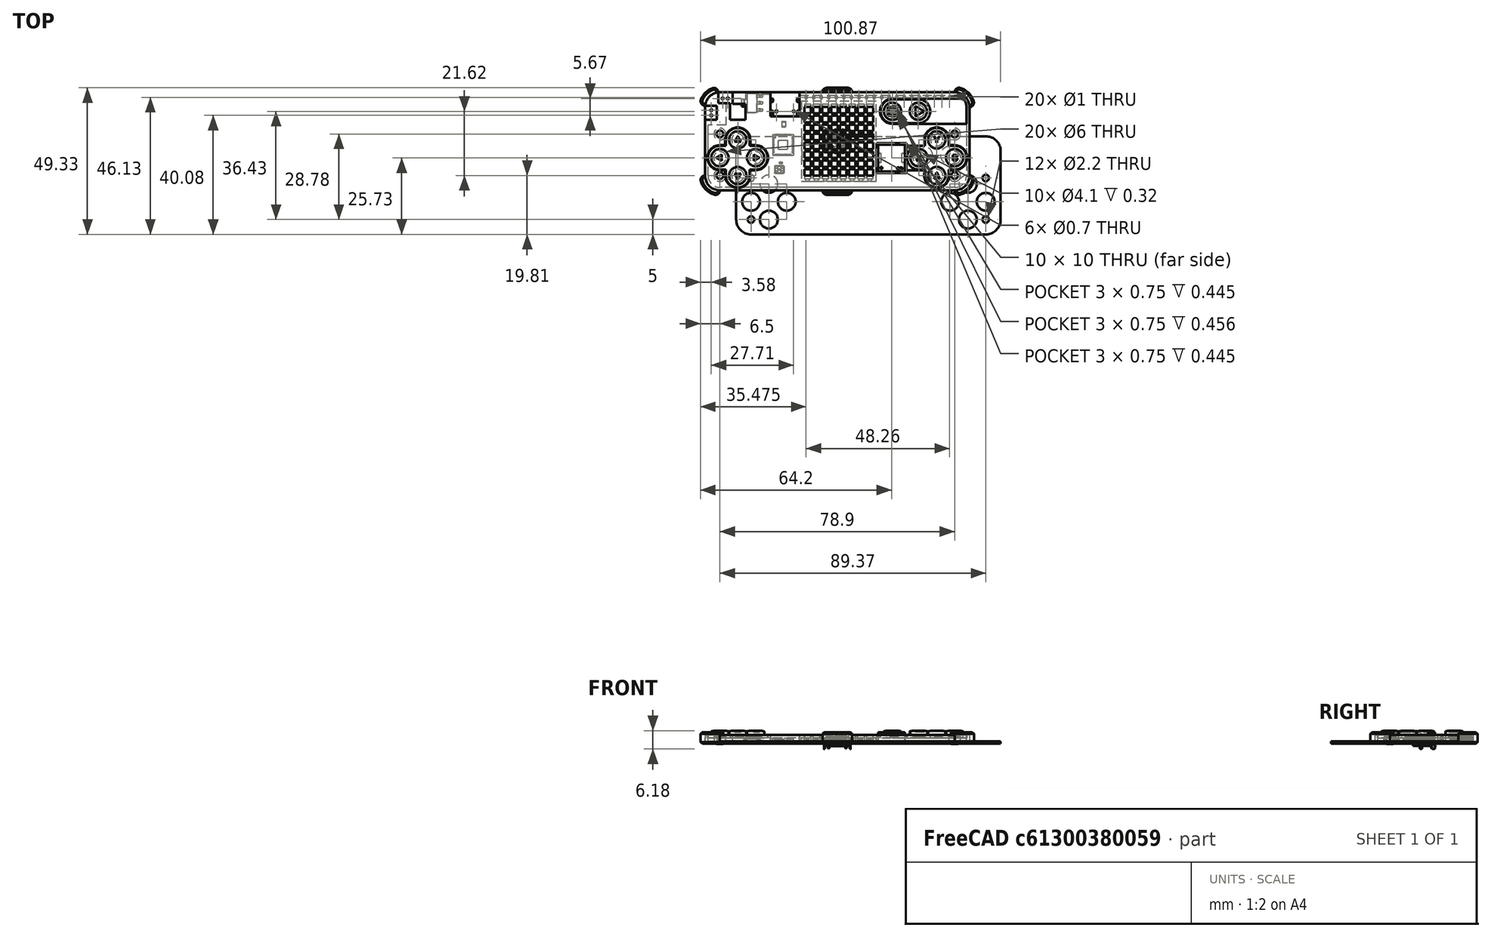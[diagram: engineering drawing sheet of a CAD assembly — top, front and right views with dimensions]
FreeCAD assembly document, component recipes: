
FREECAD ASSEMBLY — COMPONENT RECIPES ("PIX6T4_Color")

This assembly document has 8 components, labeled P0..P7 below (a component is one placed body or linked part). 4 of them carry a construction recipe — the FreeCAD feature program that regenerates the part from scratch, quoted from this document or its linked companion documents; the rest are supplied as boundary geometry only. No exploded tour is included for this assembly.
COMPONENT P0 — geometry summary ("PIX6T4_Color_top"; no construction recipe available for this part):
  bounding box: 88.9 x 33.0 x 0.8 mm
  tessellated surface: 7,652 triangles
  volume: 2030 mm^3 (86% of its bounding box)
  symmetry: mirror-symmetric across its z mid-plane
COMPONENT P1 — geometry summary ("PIX6T4_Color_top_Rev1"; no construction recipe available for this part):
  bounding box: 88.9 x 33.0 x 0.8 mm
  tessellated surface: 7,672 triangles
  volume: 1950 mm^3 (83% of its bounding box)
COMPONENT P2 — geometry summary ("PIX6T4_Color_Rev2"; no construction recipe available for this part):
  bounding box: 88.9 x 33.0 x 4.2 mm
  tessellated surface: 153,932 triangles
  volume: 3159 mm^3 (26% of its bounding box)
COMPONENT P3 — geometry summary ("PIX6T4_Color_Rev1"; no construction recipe available for this part):
  bounding box: 88.9 x 33.0 x 4.2 mm
  tessellated surface: 147,180 triangles
  volume: 3151 mm^3 (25% of its bounding box)
COMPONENT P4 — recipe-attached ("Body", modeled in this document).
Construction recipe (the document's own serialized feature program — sketch geometry with constraints, then the solid features built on it; lengths are millimeters unless a unit is written):

FEATURE [PartDesign::SubShapeBinder] Binder  label="Top of PCB Binder"
  BindCopyOnChange = 0
  BindMode = 0
  ClaimChildren = false
  Context = -> Body [Binder.]
  Fuse = false
  MakeFace = true
  OffsetFill = false
  OffsetIntersection = false
  OffsetJoinType = 0
  OffsetOpenResult = false
  PartialLoad = false
  Relative = true
  Support = -> [Board_e6d7[Board_Geoms_e6d7.Pcb_e6d7.Face63]]
  _Version = 2
FEATURE [PartDesign::Plane] DatumPlane
  AttachmentSupport = -> [Binder]
  Length = 105.452
  MapMode = 5
  ResizeMode = 0
  Width = 63.5569
FEATURE [PartDesign::SubShapeBinder] Binder001  label="Bottom of top binder"
  BindCopyOnChange = 0
  BindMode = 0
  ClaimChildren = false
  Context = -> Board_83e9 [Body.Binder001.]
  Fuse = false
  MakeFace = true
  OffsetFill = false
  OffsetIntersection = false
  OffsetJoinType = 0
  OffsetOpenResult = false
  PartialLoad = false
  Relative = true
  Support = -> [Board_83e9[Board_Geoms_83e9.Pcb_83e9.Face32]]
  _Version = 2
FEATURE [PartDesign::Plane] DatumPlane001
  AttachmentSupport = -> [Binder001]
  Length = 105.452
  MapMode = 5
  Placement = pos=(0,0,2.2) rot=(1,0,0;3.14159rad)
  ResizeMode = 0
  Width = 63.5569
FEATURE [Sketcher::SketchObject] Sketch001
  ArcFitTolerance = 1e-06
  AttachmentSupport = -> [DatumPlane001]
  ExternalGeometry = -> [Binder001]
  FullyConstrained = true
  MakeInternals = false
  MapMode = 5
  Placement = pos=(0,0,2.2) rot=(1,0,0;3.14159rad)
  sketch-geometry (44):
    g0: ArcOfCircle CenterX=18.55 CenterY=-10.11 CenterZ=0 NormalX=0 NormalY=0 NormalZ=1 AngleXU=0 Radius=4.2 StartAngle=1.5708 EndAngle=4.71239
    g1: ArcOfCircle CenterX=27.25 CenterY=-10.11 CenterZ=0 NormalX=0 NormalY=0 NormalZ=1 AngleXU=0 Radius=4.2 StartAngle=4.71239 EndAngle=7.85398
    g2: LineSegment StartX=18.55 StartY=-5.91 StartZ=0 EndX=27.25 EndY=-5.91 EndZ=0
    g3: LineSegment StartX=18.55 StartY=-14.31 StartZ=0 EndX=27.25 EndY=-14.31 EndZ=0
    g4: ArcOfCircle CenterX=-39.45 CenterY=5.51 CenterZ=0 NormalX=0 NormalY=0 NormalZ=1 AngleXU=0 Radius=4.2 StartAngle=1.5708 EndAngle=4.71239
    g5: ArcOfCircle CenterX=-33.45 CenterY=11.51 CenterZ=0 NormalX=0 NormalY=0 NormalZ=1 AngleXU=0 Radius=4.2 StartAngle=0 EndAngle=3.14159
    g6: ArcOfCircle CenterX=-27.45 CenterY=5.51 CenterZ=0 NormalX=0 NormalY=0 NormalZ=1 AngleXU=0 Radius=4.2 StartAngle=4.71239 EndAngle=7.85398
    g7: ArcOfCircle CenterX=-33.45 CenterY=-0.49 CenterZ=0 NormalX=0 NormalY=0 NormalZ=1 AngleXU=0 Radius=4.2 StartAngle=3.14159 EndAngle=6.28319
    g8: LineSegment StartX=-39.45 StartY=9.71 StartZ=0 EndX=-37.65 EndY=9.71 EndZ=0
    g9: LineSegment StartX=-37.65 StartY=9.71 StartZ=0 EndX=-37.65 EndY=11.51 EndZ=0
    g10: LineSegment StartX=-39.45 StartY=1.31 StartZ=0 EndX=-37.65 EndY=1.31 EndZ=0
    g11: LineSegment StartX=-37.65 StartY=1.31 StartZ=0 EndX=-37.65 EndY=-0.49 EndZ=0
    g12: LineSegment StartX=-29.25 StartY=-0.49 StartZ=0 EndX=-29.25 EndY=1.31 EndZ=0
    g13: LineSegment StartX=-29.25 StartY=1.31 StartZ=0 EndX=-27.45 EndY=1.31 EndZ=0
    g14: LineSegment StartX=-29.25 StartY=11.51 StartZ=0 EndX=-29.25 EndY=9.71 EndZ=0
    g15: LineSegment StartX=-29.25 StartY=9.71 StartZ=0 EndX=-27.45 EndY=9.71 EndZ=0
    g16: LineSegment StartX=-39.45 StartY=-16.51 StartZ=0 EndX=-22.45 EndY=-16.51 EndZ=0
    g17: LineSegment StartX=-22.45 StartY=-16.51 StartZ=0 EndX=-22.45 EndY=-8.46 EndZ=0
    g18: LineSegment StartX=-22.45 StartY=-8.46 StartZ=0 EndX=-12.65 EndY=-8.46 EndZ=0
    g19: LineSegment StartX=-12.65 StartY=-8.46 StartZ=0 EndX=-12.65 EndY=-16.51 EndZ=0
    g20: LineSegment StartX=-12.65 StartY=-16.51 StartZ=0 EndX=39.45 EndY=-16.51 EndZ=0
    g21: LineSegment StartX=-44.45 StartY=-11.51 StartZ=0 EndX=-44.45 EndY=11.51 EndZ=0
    g22: LineSegment StartX=-39.45 StartY=16.51 StartZ=0 EndX=39.45 EndY=16.51 EndZ=0
    g23: LineSegment StartX=13.25 StartY=10.59 StartZ=0 EndX=13.25 EndY=0.59 EndZ=0
    g24: LineSegment StartX=13.25 StartY=0.59 StartZ=0 EndX=23.25 EndY=0.59 EndZ=0
    g25: LineSegment StartX=23.25 StartY=10.59 StartZ=0 EndX=13.25 EndY=10.59 EndZ=0
    g26: LineSegment StartX=44.45 StartY=11.51 StartZ=0 EndX=44.45 EndY=-11.51 EndZ=0
    g27: ArcOfCircle CenterX=33.45 CenterY=11.51 CenterZ=0 NormalX=0 NormalY=0 NormalZ=1 AngleXU=0 Radius=4.2 StartAngle=1e-16 EndAngle=3.14159
    g28: ArcOfCircle CenterX=39.45 CenterY=5.51 CenterZ=0 NormalX=0 NormalY=0 NormalZ=1 AngleXU=0 Radius=4.2 StartAngle=4.71239 EndAngle=7.85398
    g29: ArcOfCircle CenterX=33.45 CenterY=-0.49 CenterZ=0 NormalX=0 NormalY=0 NormalZ=1 AngleXU=0 Radius=4.2 StartAngle=3.14159 EndAngle=6.28319
    g30: LineSegment StartX=23.25 StartY=9.71 StartZ=0 EndX=29.25 EndY=9.71 EndZ=0
    g31: LineSegment StartX=29.25 StartY=9.71 StartZ=0 EndX=29.25 EndY=11.51 EndZ=0
    g32: LineSegment StartX=37.65 StartY=11.51 StartZ=0 EndX=37.65 EndY=9.71 EndZ=0
    g33: LineSegment StartX=37.65 StartY=9.71 StartZ=0 EndX=39.45 EndY=9.71 EndZ=0
    g34: LineSegment StartX=39.45 StartY=1.31 StartZ=0 EndX=37.65 EndY=1.31 EndZ=0
    g35: LineSegment StartX=37.65 StartY=1.31 StartZ=0 EndX=37.65 EndY=-0.49 EndZ=0
    g36: LineSegment StartX=29.25 StartY=-0.49 StartZ=0 EndX=29.25 EndY=1.47 EndZ=0
    g37: LineSegment StartX=23.25 StartY=1.47 StartZ=0 EndX=29.25 EndY=1.47 EndZ=0
    g38: ArcOfCircle CenterX=-39.45 CenterY=11.51 CenterZ=0 NormalX=0 NormalY=0 NormalZ=1 AngleXU=0 Radius=5 StartAngle=1.5708 EndAngle=3.14159
    g39: ArcOfCircle CenterX=39.45 CenterY=11.51 CenterZ=0 NormalX=0 NormalY=0 NormalZ=1 AngleXU=0 Radius=5 StartAngle=0 EndAngle=1.5708
    g40: ArcOfCircle CenterX=39.45 CenterY=-11.51 CenterZ=0 NormalX=0 NormalY=0 NormalZ=1 AngleXU=0 Radius=5 StartAngle=4.71239 EndAngle=6.28319
    g41: ArcOfCircle CenterX=-39.45 CenterY=-11.51 CenterZ=0 NormalX=0 NormalY=0 NormalZ=1 AngleXU=0 Radius=5 StartAngle=3.14159 EndAngle=4.71239
    g42: LineSegment StartX=23.25 StartY=10.59 StartZ=0 EndX=23.25 EndY=9.71 EndZ=0
    g43: LineSegment StartX=23.25 StartY=0.59 StartZ=0 EndX=23.25 EndY=1.47 EndZ=0
  constraints (120):
    c: Tangent(g0,g2) = 1.5708
    c: Tangent(g0,g3) = -1.5708
    c: Tangent(g1,g2) = 1.5708
    c: Tangent(g1,g3) = -1.5708
    c: Coincident(g0,g-11)
    c: Coincident(g1,g-20)
    c: Coincident(g4,g-8)
    c: Coincident(g5,g-7)
    c: Coincident(g6,g-10)
    c: Coincident(g7,g-9)
    c: Horizontal(g7,g7)
    c: Horizontal(g7,g7)
    c: Vertical(g6,g6)
    c: Vertical(g6,g6)
    c: Horizontal(g5,g5)
    c: Horizontal(g5,g5)
    c: Vertical(g4,g4)
    c: Vertical(g4,g4)
    c: Tangent(g4,g8) = 1.5708
    c: Coincident(g8,g9)
    c: Vertical(g9)
    c: Coincident(g9,g5)
    c: Tangent(g4,g10) = -1.5708
    c: Coincident(g10,g11)
    c: Coincident(g11,g7)
    c: Vertical(g11)
    c: Tangent(g7,g12) = -1.5708
    c: Coincident(g12,g13)
    c: Coincident(g13,g6)
    c: Horizontal(g13)
    c: Coincident(g5,g14)
    c: Vertical(g14)
    c: Coincident(g14,g15)
    c: Coincident(g15,g6)
    c: Horizontal(g15)
    c: Coincident(g-4,g16)
    c: Horizontal(g16)
    c: Coincident(g16,g17)
    c: Coincident(g17,g-19)
    c: Vertical(g17)
    c: Coincident(g17,g18)
    c: Coincident(g18,g-19)
    c: Coincident(g18,g19)
    c: Vertical(g19)
    c: Coincident(g19,g20)
    c: Coincident(g20,g-5)
    c: Horizontal(g20)
    c: Coincident(g21,g-4)
    c: Coincident(g22,g-3)
    c: Coincident(g23,g24)
    c: Coincident(g25,g23)
    c: Vertical(g23)
    c: Horizontal(g24)
    c: Coincident(g23,g-17)
    c: Coincident(g24,g-18)
    c: Coincident(g27,g-16)
    c: Coincident(g28,g-15)
    c: Coincident(g29,g-14)
    c: Horizontal(g29,g29)
    c: Horizontal(g29,g29)
    c: Vertical(g28,g28)
    c: Vertical(g28,g28)
    c: Horizontal(g27,g27)
    c: Horizontal(g27,g27)
    c: Coincident(g31,g30)
    c: Coincident(g31,g27)
    c: Coincident(g32,g27)
    c: Coincident(g33,g32)
    c: Coincident(g33,g28)
    c: Coincident(g34,g28)
    c: Coincident(g35,g34)
    c: Coincident(g35,g29)
    c: Coincident(g36,g29)
    c: Coincident(g37,g36)
    c: Horizontal(g37)
    c: Horizontal(g30)
    c: Horizontal(g33)
    c: Horizontal(g34)
    c: Vertical(g35)
    c: Vertical(g36)
    c: Vertical(g31)
    c: Vertical(g32)
    c: Horizontal(g38,g38)
    c: Vertical(g38,g38)
    c: Coincident(g38,g21)
    c: Vertical(g21)
    c: Coincident(g38,g22)
    c: Horizontal(g41,g41)
    c: Coincident(g41,g21)
    c: Coincident(g41,g16)
    c: Vertical(g39,g39)
    c: Horizontal(g39,g39)
    c: Coincident(g39,g26)
    c: Coincident(g39,g22)
    c: Horizontal(g22)
    c: Vertical(g26)
    c: Coincident(g26,g-5)
    c: Vertical(g22,g20)
    c: Horizontal(g40,g40)
    c: Coincident(g40,g26)
    c: Coincident(g40,g20)
    c: Horizontal(g2)
    c: Distance(g-20,g1) = 1.2
    c: Equal(g6,g5)
    c: Equal(g6,g7)
    c: Equal(g4,g7)
    c: Equal(g27,g28)
    c: Equal(g28,g29)
    c: Coincident(g42,g25)
    c: Vertical(g42)
    c: Coincident(g43,g24)
    c: Vertical(g43)
    c: Coincident(g30,g42)
    c: Coincident(g25,g-17)
    c: Coincident(g37,g43)
    c: Equal(g42,g43)
    c: Horizontal(g30,g32)
    c: Distance(g-15,g28) = 1.2
    c: Distance(g-8,g4) = 1.2
    c: Distance(g-8,g21) = 2  'EdgeToButton'
FEATURE [PartDesign::Pad] Pad  label="Main pad"
  Direction = (0,0,-1)
  Length = 1
  Length2 = 10
  Placement = pos=(0,0,2.2) rot=(1,0,0;3.14159rad)
  Profile = -> Sketch001
  ReferenceAxis = -> Sketch001 [N_Axis]
  Suppressed = false
  Type = 0
FEATURE [PartDesign::SubShapeBinder] Binder002  label="LED Binder"
  BindCopyOnChange = 0
  BindMode = 0
  ClaimChildren = false
  Context = -> Body [Binder002.]
  Fuse = false
  MakeFace = true
  OffsetFill = false
  OffsetIntersection = false
  OffsetJoinType = 0
  OffsetOpenResult = false
  PartialLoad = false
  Relative = true
  Support = -> [Board_e6d7[Step_Models_e6d7.Top_e6d7.D13_LED_SMD_4P_L1_4_W1_4_TL007_e765e95fd25d_ln_051.Part__Feature005.Face6,Step_Models_e6d7.Top_e6d7.D13_LED_SMD_4P_L1_4_W1_4_TL007_e765e95fd25d_ln_030.Part__Feature005.Face6,Step_Models_e6d7.Top_e6d7.D13_LED_SMD_4P_L1_4_W1_4_TL007_e765e95fd25d_ln_048.Part__Feature005.Face6,Step_Models_e6d7.Top_e6d7.D13_LED_SMD_4P_L1_4_W1_4_TL007_e765e95fd25d_ln_010.Part__Feature005.Face6]]
  _Version = 2
FEATURE [Sketcher::SketchObject] Sketch
  ArcFitTolerance = 1e-06
  AttachmentSupport = -> [DatumPlane]
  ExternalGeometry = -> [Binder,Binder001,Binder002]
  FullyConstrained = true
  MakeInternals = false
  MapMode = 5
  sketch-geometry (49):
    g0: ArcOfCircle CenterX=-39.45 CenterY=11.51 CenterZ=0 NormalX=0 NormalY=0 NormalZ=1 AngleXU=0 Radius=5.02299 StartAngle=1.68051 EndAngle=3.04589
    g1: LineSegment StartX=-44.45 StartY=11.99 StartZ=0 EndX=-40.8839 EndY=11.99 EndZ=0
    g2: LineSegment StartX=-40 StartY=16.5028 StartZ=0 EndX=-40 EndY=12.8739 EndZ=0
    g3: LineSegment StartX=-35.2 StartY=14.5028 StartZ=0 EndX=-35.2 EndY=16.5028 EndZ=0
    g4: LineSegment StartX=-22.45 StartY=16.51 StartZ=0 EndX=-22.45 EndY=15.76 EndZ=0
    g5: LineSegment StartX=-22.45 StartY=15.76 StartZ=0 EndX=-26.7 EndY=15.76 EndZ=0
    g6: LineSegment StartX=-35.2 StartY=14.5028 StartZ=0 EndX=-30.7 EndY=14.5028 EndZ=0
    g7: LineSegment StartX=-12.65 StartY=16.51 StartZ=0 EndX=39.45 EndY=16.51 EndZ=0
    g8: ArcOfCircle CenterX=39.45 CenterY=11.51 CenterZ=0 NormalX=0 NormalY=0 NormalZ=1 AngleXU=0 Radius=5 StartAngle=0 EndAngle=1.5708
    g9: ArcOfCircle CenterX=39.45 CenterY=-11.51 CenterZ=0 NormalX=0 NormalY=0 NormalZ=1 AngleXU=0 Radius=5 StartAngle=4.71239 EndAngle=6.28319
    g10: ArcOfCircle CenterX=-39.45 CenterY=-11.51 CenterZ=0 NormalX=0 NormalY=0 NormalZ=1 AngleXU=0 Radius=5 StartAngle=3.14159 EndAngle=4.71239
    g11: LineSegment StartX=44.45 StartY=11.51 StartZ=0 EndX=44.45 EndY=-11.51 EndZ=0
    g12: LineSegment StartX=39.45 StartY=-16.51 StartZ=0 EndX=-39.45 EndY=-16.51 EndZ=0
    g13: LineSegment StartX=-44.45 StartY=-11.51 StartZ=0 EndX=-44.45 EndY=7.24 EndZ=0
    g14: LineSegment StartX=-12.65 StartY=16.51 StartZ=0 EndX=-12.65 EndY=15.51 EndZ=0
    g15: LineSegment StartX=-12.65 StartY=15.51 StartZ=0 EndX=39.45 EndY=15.51 EndZ=0
    g16: ArcOfCircle CenterX=39.45 CenterY=11.51 CenterZ=0 NormalX=0 NormalY=0 NormalZ=1 AngleXU=0 Radius=4 StartAngle=1e-16 EndAngle=1.5708
    g17: LineSegment StartX=43.45 StartY=11.51 StartZ=0 EndX=43.45 EndY=-11.51 EndZ=0
    g18: ArcOfCircle CenterX=39.45 CenterY=-11.51 CenterZ=0 NormalX=0 NormalY=0 NormalZ=1 AngleXU=0 Radius=4 StartAngle=4.71239 EndAngle=6.28319
    g19: LineSegment StartX=39.45 StartY=-15.51 StartZ=0 EndX=-39.45 EndY=-15.51 EndZ=0
    g20: ArcOfCircle CenterX=-39.45 CenterY=-11.51 CenterZ=0 NormalX=0 NormalY=0 NormalZ=1 AngleXU=0 Radius=4 StartAngle=3.14159 EndAngle=4.71239
    g21: LineSegment StartX=-43.45 StartY=-11.51 StartZ=0 EndX=-43.45 EndY=5.49 EndZ=0
    g22: LineSegment StartX=-35.2 StartY=16.5028 StartZ=0 EndX=-30.7 EndY=16.5028 EndZ=0
    g23: LineSegment StartX=-26.7 StartY=16.51 StartZ=0 EndX=-22.45 EndY=16.51 EndZ=0
    g24: LineSegment StartX=-30.7 StartY=14.5028 StartZ=0 EndX=-30.7 EndY=16.5028 EndZ=0
    g25: LineSegment StartX=-26.7 StartY=16.51 StartZ=0 EndX=-26.7 EndY=15.76 EndZ=0
    g26: Circle CenterX=-39.45 CenterY=2.46 CenterZ=0 NormalX=0 NormalY=0 NormalZ=1 AngleXU=0 Radius=2
    g27: Circle CenterX=-39.45 CenterY=-11.51 CenterZ=0 NormalX=0 NormalY=0 NormalZ=1 AngleXU=0 Radius=2
    g28: Circle CenterX=39.45 CenterY=2.46 CenterZ=0 NormalX=0 NormalY=0 NormalZ=1 AngleXU=0 Radius=2
    g29: Circle CenterX=39.45 CenterY=-11.51 CenterZ=0 NormalX=0 NormalY=0 NormalZ=1 AngleXU=0 Radius=2
    g30: LineSegment StartX=-11.08 StartY=12.5 StartZ=0 EndX=-11.08 EndY=-12.5 EndZ=0
    g31: LineSegment StartX=-11.08 StartY=-12.5 StartZ=0 EndX=12.12 EndY=-12.5 EndZ=0
    g32: LineSegment StartX=12.12 StartY=-12.5 StartZ=0 EndX=12.12 EndY=12.5 EndZ=0
    g33: LineSegment StartX=12.12 StartY=12.5 StartZ=0 EndX=-11.08 EndY=12.5 EndZ=0
    g34: GeomPoint [constr] X=0.52 Y=-1.3e-15 Z=0
    g35: GeomPoint X=-10.68 Y=11.2 Z=0
    g36: GeomPoint X=11.72 Y=-11.2 Z=0
    g37: GeomPoint X=0.52 Y=-1.3e-15 Z=0
    g38: LineSegment StartX=-12.08 StartY=13.5 StartZ=0 EndX=-12.08 EndY=-13.5 EndZ=0
    g39: LineSegment StartX=-12.08 StartY=-13.5 StartZ=0 EndX=13.12 EndY=-13.5 EndZ=0
    g40: LineSegment StartX=13.12 StartY=-13.5 StartZ=0 EndX=13.12 EndY=13.5 EndZ=0
    g41: LineSegment StartX=13.12 StartY=13.5 StartZ=0 EndX=-12.08 EndY=13.5 EndZ=0
    g42: LineSegment StartX=-44.45 StartY=7.24 StartZ=0 EndX=-40.45 EndY=7.24 EndZ=0
    g43: LineSegment [constr] StartX=-40.8839 StartY=11.99 StartZ=0 EndX=-40 EndY=12.8739 EndZ=0
    g44: LineSegment StartX=-40.8839 StartY=11.99 StartZ=0 EndX=-40.45 EndY=11.5561 EndZ=0
    g45: LineSegment StartX=-40.45 StartY=11.5561 StartZ=0 EndX=-40.45 EndY=7.24 EndZ=0
    g46: LineSegment StartX=-40 StartY=12.8739 StartZ=0 EndX=-37.45 EndY=12.8739 EndZ=0
    g47: LineSegment StartX=-37.45 StartY=12.8739 StartZ=0 EndX=-37.45 EndY=5.49 EndZ=0
    g48: LineSegment StartX=-37.45 StartY=5.49 StartZ=0 EndX=-43.45 EndY=5.49 EndZ=0
  constraints (127):
    c: Coincident(g0,g-3)
    c: Vertical(g0,g-3)
    c: Horizontal(g1)
    c: Vertical(g2)
    c: Vertical(g3)
    c: Coincident(g3,g22)
    c: Coincident(g23,g-7)
    c: Coincident(g23,g4)
    c: PointOnObject(g4,g-7)
    c: Coincident(g4,g5)
    c: Horizontal(g5)
    c: DistanceX(g22,g23) = 12.75
    c: Coincident(g3,g6)
    c: Horizontal(g6)
    c: Coincident(g-9,g7)
    c: Coincident(g7,g-4)
    c: Coincident(g8,g-4)
    c: Horizontal(g8,g8)
    c: Coincident(g8,g7)
    c: Coincident(g9,g-5)
    c: Coincident(g9,g-5)
    c: Coincident(g11,g8)
    c: Coincident(g13,g10)
    c: Vertical(g13)
    c: Coincident(g11,g9)
    c: Coincident(g12,g9)
    c: Coincident(g12,g10)
    c: Coincident(g10,g-6)
    c: Coincident(g7,g14)
    c: PointOnObject(g14,g-9)
    c: Coincident(g14,g15)
    c: Horizontal(g15)
    c: DistanceY(g14,g14) = 1
    c: Coincident(g16,g8)
    c: Coincident(g16,g15)
    c: Horizontal(g8,g16)
    c: Coincident(g17,g16)
    c: Vertical(g17)
    c: Coincident(g18,g9)
    c: Coincident(g18,g17)
    c: Horizontal(g9,g17)
    c: Vertical(g9,g18)
    c: Coincident(g19,g18)
    c: Horizontal(g19)
    c: Coincident(g20,g10)
    c: Coincident(g20,g19)
    c: Coincident(g10,g-6)
    c: Horizontal(g20,g10)
    c: Coincident(g21,g20)
    c: Vertical(g21)
    c: Vertical(g10,g19)
    c: Vertical(g15,g8)
    c: DistanceY(g13,g0) = 4.75
    c: Horizontal(g22)
    c: Horizontal(g23)
    c: Coincident(g24,g6)
    c: Coincident(g24,g22)
    c: Vertical(g24)
    c: Horizontal(g0,g3)
    c: DistanceX(g22,g22) = 4.5
    c: DistanceX(g23,g23) = 4.25
    c: Coincident(g25,g23)
    c: Coincident(g25,g5)
    c: Vertical(g25)
    c: DistanceY(g25,g25) = 0.75
    c: Vertical(g10,g10)
    c: Horizontal(g9,g9)
    c: Diameter(g26) = 4
    c: Coincident(g26,g-10)
    c: Coincident(g27,g10)
    c: Coincident(g28,g-12)
    c: Coincident(g29,g9)
    c: Equal(g26,g27)
    c: Equal(g26,g28)
    c: Equal(g26,g29)
    c: Coincident(g30,g31)
    c: Coincident(g31,g32)
    c: Coincident(g32,g33)
    c: Coincident(g33,g30)
    c: Vertical(g30)
    c: Vertical(g32)
    c: Horizontal(g31)
    c: Horizontal(g33)
    c: Coincident(g35,g-14)
    c: Coincident(g36,g-15)
    c: Coincident(g37,g34)
    c: Symmetric(g35,g36,g34)
    c: Symmetric(g30,g31,g34)
    c: Coincident(g38,g39)
    c: Coincident(g39,g40)
    c: Coincident(g40,g41)
    c: Coincident(g41,g38)
    c: Vertical(g38)
    c: Vertical(g40)
    c: Horizontal(g39)
    c: Horizontal(g41)
    c: Symmetric(g38,g39,g34)
    c: DistanceY(g32,g40) = 1
    c: DistanceX(g33,g33) = 23.2
    c: DistanceY(g32,g32) = 25
    c: DistanceX(g38,g30) = 1
    c: DistanceY(g13,g13) = 18.75
    c: Coincident(g1,g0)
    c: DistanceX(g0,g3) = 4.8
    c: Coincident(g2,g0)
    c: DistanceY(g3,g3) = 2
    c: Coincident(g42,g13)
    c: Horizontal(g42)
    c: Coincident(g43,g1)
    c: Coincident(g43,g2)
    c: Angle(g1,g43) = 0.785398
    c: Distance(g43,g43) = 1.25
    c: Coincident(g1,g44)
    c: Coincident(g44,g45)
    c: Vertical(g45)
    c: Coincident(g2,g46)
    c: Horizontal(g46)
    c: Coincident(g46,g47)
    c: Vertical(g47)
    c: Coincident(g47,g48)
    c: Horizontal(g48)
    c: Coincident(g45,g42)
    c: Coincident(g21,g48)
    c: DistanceY(g21,g13) = 1.75
    c: Perpendicular(g43,g44)
    c: DistanceX(g42,g42) = 4
    c: DistanceX(g48,g48) = 6
FEATURE [PartDesign::Pad] Pad001  label="Walls"
  BaseFeature = -> Pad
  Direction = (0,0,1)
  Length = 10
  Length2 = 10
  Placement = pos=(0,0,2.2) rot=(1,0,0;3.14159rad)
  Profile = -> Sketch
  ReferenceAxis = -> Sketch [N_Axis]
  Refine = true
  Suppressed = false
  Type = 3
  UpToFace = -> Pad [Face46]
FEATURE [Sketcher::SketchObject] Sketch002
  ArcFitTolerance = 1e-06
  AttachmentSupport = -> [Pad]
  ExternalGeometry = -> [Binder002]
  FullyConstrained = true
  MakeInternals = false
  MapMode = 5
  Placement = pos=(0,0,1.2) rot=(1,0,0;3.14159rad)
  sketch-geometry (9):
    g0: GeomPoint [constr] X=-9.98 Y=10.5 Z=0
    g1: LineSegment StartX=-11.08 StartY=11.6 StartZ=0 EndX=-11.08 EndY=9.4 EndZ=0
    g2: LineSegment StartX=-11.08 StartY=9.4 StartZ=0 EndX=-8.88 EndY=9.4 EndZ=0
    g3: LineSegment StartX=-8.88 StartY=9.4 StartZ=0 EndX=-8.88 EndY=11.6 EndZ=0
    g4: LineSegment StartX=-8.88 StartY=11.6 StartZ=0 EndX=-11.08 EndY=11.6 EndZ=0
    g5: LineSegment StartX=-11.48 StartY=12 StartZ=0 EndX=-11.48 EndY=9 EndZ=0
    g6: LineSegment StartX=-11.48 StartY=9 StartZ=0 EndX=-8.48 EndY=9 EndZ=0
    g7: LineSegment StartX=-8.48 StartY=9 StartZ=0 EndX=-8.48 EndY=12 EndZ=0
    g8: LineSegment StartX=-8.48 StartY=12 StartZ=0 EndX=-11.48 EndY=12 EndZ=0
  constraints (23):
    c: Symmetric(g-3,g-4,g0)
    c: Coincident(g1,g2)
    c: Coincident(g2,g3)
    c: Coincident(g3,g4)
    c: Coincident(g4,g1)
    c: Vertical(g1)
    c: Vertical(g3)
    c: Horizontal(g2)
    c: Horizontal(g4)
    c: Equal(g2,g3)
    c: Symmetric(g1,g2,g0)
    c: Coincident(g5,g6)
    c: Coincident(g6,g7)
    c: Coincident(g7,g8)
    c: Coincident(g8,g5)
    c: Vertical(g5)
    c: Vertical(g7)
    c: Horizontal(g6)
    c: Horizontal(g8)
    c: Equal(g6,g7)
    c: Symmetric(g5,g6,g0)
    c: DistanceY(g3,g7) = 0.4
    c: DistanceX(g8,g8) = 3
FEATURE [PartDesign::Pocket] Pocket  label="Single LED Pocket"
  BaseFeature = -> Pad001
  Direction = (0,0,1)
  Length = 5
  Length2 = 5
  Placement = pos=(0,0,2.2) rot=(1,0,0;3.14159rad)
  Profile = -> Sketch002 [Edge1,Edge2,Edge3,Edge4]
  ReferenceAxis = -> Sketch002 [N_Axis]
  Suppressed = false
  Type = 1
FEATURE [PartDesign::LinearPattern] LinearPattern
  Direction = -> Sketch002 [H_Axis]
  Length = 21
  Mode = 1
  Occurrences = 8
  Offset = 3
  Placement = pos=(0,0,2.2) rot=(1,0,0;3.14159rad)
  Suppressed = false
  TransformMode = 0
FEATURE [PartDesign::LinearPattern] LinearPattern001
  Direction = -> Sketch002 [V_Axis]
  Length = 21
  Mode = 1
  Occurrences = 8
  Offset = 3
  Placement = pos=(0,0,2.2) rot=(1,0,0;3.14159rad)
  Reversed = true
  Suppressed = false
  TransformMode = 0
FEATURE [PartDesign::MultiTransform] MultiTransform  label="All LED pockets MultiTransform"
  BaseFeature = -> Pocket
  Originals = -> [Pocket]
  Placement = pos=(0,0,2.2) rot=(1,0,0;3.14159rad)
  Suppressed = false
  TransformMode = 0
  Transformations = -> [LinearPattern,LinearPattern001]
FEATURE [Sketcher::SketchObject] Sketch003
  ArcFitTolerance = 1e-06
  AttachmentSupport = -> [MultiTransform]
  ExternalGeometry = -> [Binder001]
  FullyConstrained = true
  MakeInternals = false
  MapMode = 5
  Placement = pos=(0,0,0) rot=(1,0,0;3.14159rad)
  sketch-geometry (4):
    g0: Circle CenterX=-39.45 CenterY=11.51 CenterZ=0 NormalX=0 NormalY=0 NormalZ=1 AngleXU=0 Radius=1.15
    g1: Circle CenterX=-39.45 CenterY=-2.46 CenterZ=0 NormalX=0 NormalY=0 NormalZ=1 AngleXU=0 Radius=1.15
    g2: Circle CenterX=39.45 CenterY=11.51 CenterZ=0 NormalX=0 NormalY=0 NormalZ=1 AngleXU=0 Radius=1.15
    g3: Circle CenterX=39.45 CenterY=-2.46 CenterZ=0 NormalX=0 NormalY=0 NormalZ=1 AngleXU=0 Radius=1.15
  constraints (8):
    c: Coincident(g0,g-3)
    c: Coincident(g1,g-4)
    c: Coincident(g2,g-5)
    c: Coincident(g3,g-6)
    c: Equal(g0,g1)
    c: Equal(g0,g2)
    c: Equal(g0,g3)
    c: Distance(g-3,g0) = 0.05
FEATURE [PartDesign::Pad] Pad002  label="Bottom pillars"
  BaseFeature = -> MultiTransform
  Direction = (0,0,-1)
  Length = 0.9
  Length2 = 10
  Placement = pos=(0,0,2.2) rot=(1,0,0;3.14159rad)
  Profile = -> Sketch003
  ReferenceAxis = -> Sketch003 [N_Axis]
  Suppressed = false
  Type = 0
FEATURE [Sketcher::SketchObject] Sketch004
  ArcFitTolerance = 1e-06
  AttachmentSupport = -> [Pad002]
  ExternalGeometry = -> [Pad002]
  FullyConstrained = true
  MakeInternals = false
  MapMode = 5
  Placement = pos=(0,0,2.2) rot=(0,0,1;0rad)
  sketch-geometry (4):
    g0: Circle CenterX=-39.45 CenterY=2.46 CenterZ=0 NormalX=0 NormalY=0 NormalZ=1 AngleXU=0 Radius=1.15
    g1: Circle CenterX=-39.45 CenterY=-11.51 CenterZ=0 NormalX=0 NormalY=0 NormalZ=1 AngleXU=0 Radius=1.15
    g2: Circle CenterX=39.45 CenterY=2.46 CenterZ=0 NormalX=0 NormalY=0 NormalZ=1 AngleXU=0 Radius=1.15
    g3: Circle CenterX=39.45 CenterY=-11.51 CenterZ=0 NormalX=0 NormalY=0 NormalZ=1 AngleXU=0 Radius=1.15
  constraints (8):
    c: Coincident(g0,g-5)
    c: Equal(g0,g-5)
    c: Coincident(g1,g-6)
    c: Equal(g1,g-6)
    c: Coincident(g2,g-3)
    c: Equal(g2,g-3)
    c: Coincident(g3,g-4)
    c: Equal(g3,g-4)
FEATURE [PartDesign::Pad] Pad003  label="Top pillars"
  BaseFeature = -> Pad002
  Direction = (0,0,1)
  Length = 0.9
  Length2 = 10
  Placement = pos=(0,0,2.2) rot=(1,0,0;3.14159rad)
  Profile = -> Sketch004
  ReferenceAxis = -> Sketch004 [N_Axis]
  Suppressed = false
  Type = 0
FEATURE [Sketcher::SketchObject] Sketch005
  ArcFitTolerance = 1e-06
  AttachmentSupport = -> [Pad003]
  ExternalGeometry = -> [Pad003]
  FullyConstrained = true
  MakeInternals = false
  MapMode = 5
  Placement = pos=(0,0,2.2) rot=(0,0,1;0rad)
  sketch-geometry (25):
    g0: LineSegment [constr] StartX=-30.7 StartY=17.01 StartZ=0 EndX=-30.7 EndY=9.50278 EndZ=0
    g1: LineSegment [constr] StartX=-30.7 StartY=9.50278 StartZ=0 EndX=-26.7 EndY=9.50278 EndZ=0
    g2: LineSegment [constr] StartX=-26.7 StartY=9.50278 StartZ=0 EndX=-26.7 EndY=17.01 EndZ=0
    g3: LineSegment [constr] StartX=-29.2893 StartY=8.35468 StartZ=0 EndX=-29.2893 EndY=2.70524 EndZ=0
    g4: LineSegment [constr] StartX=-29.2893 StartY=2.70524 StartZ=0 EndX=-23.6663 EndY=2.70524 EndZ=0
    g5: LineSegment [constr] StartX=-23.6663 StartY=2.70524 StartZ=0 EndX=-23.6663 EndY=8.35468 EndZ=0
    g6: LineSegment [constr] StartX=-23.6663 StartY=8.35468 StartZ=0 EndX=-29.2893 EndY=8.35468 EndZ=0
    g7: LineSegment [constr] StartX=-22.1254 StartY=2.76229 StartZ=0 EndX=-22.1254 EndY=-5.05961 EndZ=0
    g8: LineSegment [constr] StartX=-22.1254 StartY=-5.05961 StartZ=0 EndX=-14.3474 EndY=-5.05961 EndZ=0
    g9: LineSegment [constr] StartX=-14.3474 StartY=-5.05961 StartZ=0 EndX=-14.3474 EndY=2.76229 EndZ=0
    g10: LineSegment [constr] StartX=-14.3474 StartY=2.76229 StartZ=0 EndX=-22.1254 EndY=2.76229 EndZ=0
    g11: LineSegment StartX=-44.45 StartY=11.99 StartZ=0 EndX=-44.45 EndY=7.24 EndZ=0
    g12: LineSegment StartX=-44.45 StartY=7.24 StartZ=0 EndX=-40.45 EndY=7.24 EndZ=0
    g13: LineSegment StartX=-40.45 StartY=7.24 StartZ=0 EndX=-40.45 EndY=11.99 EndZ=0
    g14: LineSegment StartX=-40.45 StartY=11.99 StartZ=0 EndX=-44.45 EndY=11.99 EndZ=0
    g15: LineSegment [constr] StartX=-30.7 StartY=17.01 StartZ=0 EndX=-26.7 EndY=17.01 EndZ=0
    g16: LineSegment StartX=-35.2 StartY=17.01 StartZ=0 EndX=-40 EndY=17.01 EndZ=0
    g17: LineSegment StartX=-40 StartY=17.01 StartZ=0 EndX=-40 EndY=12.8739 EndZ=0
    g18: LineSegment StartX=-35.2 StartY=12.56 StartZ=0 EndX=-35.2 EndY=17.01 EndZ=0
    g19: LineSegment StartX=-36.1 StartY=12.8739 StartZ=0 EndX=-36.1 EndY=7.26 EndZ=0
    g20: LineSegment StartX=-36.1 StartY=7.26 StartZ=0 EndX=-30.8 EndY=7.26 EndZ=0
    g21: LineSegment StartX=-30.8 StartY=7.26 StartZ=0 EndX=-30.8 EndY=12.56 EndZ=0
    g22: GeomPoint [constr] X=-33.45 Y=9.91 Z=0
    g23: LineSegment StartX=-40 StartY=12.8739 StartZ=0 EndX=-36.1 EndY=12.8739 EndZ=0
    g24: LineSegment StartX=-30.8 StartY=12.56 StartZ=0 EndX=-35.2 EndY=12.56 EndZ=0
  constraints (66):
    c: Coincident(g1,g2)
    c: Vertical(g0)
    c: Vertical(g2)
    c: Horizontal(g1)
    c: Coincident(g3,g4)
    c: Coincident(g4,g5)
    c: Coincident(g5,g6)
    c: Coincident(g6,g3)
    c: Vertical(g3)
    c: Vertical(g5)
    c: Horizontal(g4)
    c: Horizontal(g6)
    c: Coincident(g7,g8)
    c: Coincident(g8,g9)
    c: Coincident(g9,g10)
    c: Coincident(g10,g7)
    c: Vertical(g7)
    c: Vertical(g9)
    c: Horizontal(g8)
    c: Horizontal(g10)
    c: Block(g6)
    c: Block(g4)
    c: Block(g10)
    c: Block(g8)
    c: Coincident(g11,g12)
    c: Coincident(g12,g13)
    c: Coincident(g13,g14)
    c: Coincident(g14,g11)
    c: Vertical(g11)
    c: Vertical(g13)
    c: Horizontal(g12)
    c: Horizontal(g14)
    c: Coincident(g11,g-5)
    c: Coincident(g12,g-7)
    c: PointOnObject(g-4,g2)
    c: DistanceY(g-4,g2) = 0.5
    c: DistanceY(g1,g-3) = 7
    c: Coincident(g0,g1)
    c: Coincident(g15,g0)
    c: Coincident(g15,g2)
    c: Horizontal(g15)
    c: PointOnObject(g-3,g0)
    c: Coincident(g16,g17)
    c: Coincident(g17,g23)
    c: Coincident(g18,g16)
    c: Horizontal(g16)
    c: Vertical(g17)
    c: Vertical(g18)
    c: Coincident(g17,g-9)
    c: PointOnObject(g-8,g18)
    c: Horizontal(g16,g0)
    c: Coincident(g19,g20)
    c: Coincident(g20,g21)
    c: Coincident(g21,g24)
    c: Vertical(g19)
    c: Vertical(g21)
    c: Horizontal(g20)
    c: DistanceX(g19,g24) = 5.3
    c: Vertical(g22,g-10)
    c: DistanceY(g-10,g22) = 9.42
    c: Horizontal(g23)
    c: Horizontal(g24)
    c: Equal(g21,g20)
    c: Coincident(g18,g24)
    c: Symmetric(g19,g21,g22)
    c: Coincident(g19,g23)
FEATURE [PartDesign::Pocket] Pocket001  label="Left side components pockets"
  BaseFeature = -> Pad003
  Direction = (0,0,-1)
  Length = 5
  Length2 = 5
  Placement = pos=(0,0,2.2) rot=(1,0,0;3.14159rad)
  Profile = -> Sketch005
  ReferenceAxis = -> Sketch005 [N_Axis]
  Refine = true
  Suppressed = false
  Type = 1
FEATURE [Sketcher::SketchObject] Sketch014
  ArcFitTolerance = 1e-06
  AttachmentSupport = -> [Pocket001]
  ExternalGeometry = -> [Pocket001]
  FullyConstrained = true
  MakeInternals = false
  MapMode = 5
  Placement = pos=(0,0,1.2) rot=(1,0,0;3.14159rad)
  sketch-geometry (12):
    g0: LineSegment StartX=-8.88 StartY=-8.6 StartZ=0 EndX=-8.88 EndY=-5.5 EndZ=0
    g1: LineSegment StartX=-8.88 StartY=-5.5 StartZ=0 EndX=-8.08 EndY=-5.5 EndZ=0
    g2: LineSegment StartX=-8.08 StartY=-5.5 StartZ=0 EndX=-8.08 EndY=-8.6 EndZ=0
    g3: LineSegment StartX=-8.08 StartY=-8.6 StartZ=0 EndX=-4.98 EndY=-8.6 EndZ=0
    g4: LineSegment StartX=-4.98 StartY=-8.6 StartZ=0 EndX=-4.98 EndY=-9.4 EndZ=0
    g5: LineSegment StartX=-4.98 StartY=-9.4 StartZ=0 EndX=-8.08 EndY=-9.4 EndZ=0
    g6: LineSegment StartX=-8.08 StartY=-9.4 StartZ=0 EndX=-8.08 EndY=-12.5 EndZ=0
    g7: LineSegment StartX=-8.08 StartY=-12.5 StartZ=0 EndX=-8.88 EndY=-12.5 EndZ=0
    g8: LineSegment StartX=-8.88 StartY=-12.5 StartZ=0 EndX=-8.88 EndY=-9.4 EndZ=0
    g9: LineSegment StartX=-8.88 StartY=-9.4 StartZ=0 EndX=-11.98 EndY=-9.4 EndZ=0
    g10: LineSegment StartX=-11.98 StartY=-9.4 StartZ=0 EndX=-11.98 EndY=-8.6 EndZ=0
    g11: LineSegment StartX=-11.98 StartY=-8.6 StartZ=0 EndX=-8.88 EndY=-8.6 EndZ=0
  constraints (34):
    c: Coincident(g0,g-3)
    c: Vertical(g0)
    c: Coincident(g0,g1)
    c: Horizontal(g1)
    c: Coincident(g1,g2)
    c: Vertical(g2)
    c: Coincident(g2,g3)
    c: Horizontal(g3)
    c: Coincident(g3,g4)
    c: Vertical(g4)
    c: Coincident(g4,g5)
    c: Coincident(g5,g6)
    c: Vertical(g6)
    c: Coincident(g6,g7)
    c: Horizontal(g7)
    c: Coincident(g7,g8)
    c: Vertical(g8)
    c: Coincident(g8,g9)
    c: Horizontal(g9)
    c: Coincident(g9,g10)
    c: Vertical(g10)
    c: Coincident(g10,g11)
    c: Coincident(g11,g0)
    c: Horizontal(g5)
    c: Vertical(g0,g8)
    c: Horizontal(g8,g5)
    c: Horizontal(g0,g2)
    c: Vertical(g2,g5)
    c: Equal(g11,g0)
    c: Equal(g11,g3)
    c: Equal(g11,g8)
    c: PointOnObject(g7,g-4)
    c: Coincident(g5,g-5)
    c: Horizontal(g11)
FEATURE [PartDesign::Pad] Pad006  label="Matrix pillar"
  BaseFeature = -> Pocket001
  Direction = (0,0,-1)
  Length = 10
  Length2 = 10
  Placement = pos=(0,0,2.2) rot=(1,0,0;3.14159rad)
  Profile = -> Sketch014
  ReferenceAxis = -> Sketch014 [N_Axis]
  Suppressed = false
  Type = 3
  UpToFace = -> Pocket001 [Face340]
FEATURE [PartDesign::LinearPattern] LinearPattern004
  Direction = -> Sketch014 [H_Axis]
  Length = 18
  Mode = 1
  Occurrences = 7
  Offset = 3
  Placement = pos=(0,0,2.2) rot=(1,0,0;3.14159rad)
  Suppressed = false
  TransformMode = 0
FEATURE [PartDesign::LinearPattern] LinearPattern005
  Direction = -> Sketch014 [V_Axis]
  Length = 18
  Mode = 1
  Occurrences = 7
  Offset = 3
  Placement = pos=(0,0,2.2) rot=(1,0,0;3.14159rad)
  Suppressed = false
  TransformMode = 0
FEATURE [PartDesign::MultiTransform] MultiTransform001  label="Matrix pillars transform"
  BaseFeature = -> Pad006
  Originals = -> [Pad006]
  Placement = pos=(0,0,2.2) rot=(1,0,0;3.14159rad)
  Refine = true
  Suppressed = false
  TransformMode = 0
  Transformations = -> [LinearPattern004,LinearPattern005]
FEATURE [PartDesign::SubShapeBinder] Binder009  label="Logo LED Binder"
  BindCopyOnChange = 0
  BindMode = 0
  ClaimChildren = false
  Context = -> Body [Binder009.]
  Fuse = false
  MakeFace = true
  OffsetFill = false
  OffsetIntersection = false
  OffsetJoinType = 0
  OffsetOpenResult = false
  PartialLoad = false
  Relative = true
  Support = -> [Board_e6d008[Step_Models_e6d008.Top_e6d008.D13_LED_SMD_4P_L1_4_W1_4_TL007_e765e95fd25d_ln_097.]]
  _Version = 2
FEATURE [PartDesign::SubShapeBinder] Binder010  label="Second Logo LED Binder"
  BindCopyOnChange = 0
  BindMode = 0
  ClaimChildren = false
  Context = -> Body [Binder010.]
  Fuse = false
  MakeFace = true
  OffsetFill = false
  OffsetIntersection = false
  OffsetJoinType = 0
  OffsetOpenResult = false
  PartialLoad = false
  Relative = true
  Support = -> [Board_e6d008[Step_Models_e6d008.Top_e6d008.D13_LED_SMD_4P_L1_4_W1_4_TL007_e765e95fd25d_ln_082.]]
  _Version = 2
FEATURE [Sketcher::SketchObject] Sketch015
  ArcFitTolerance = 1e-06
  AttachmentSupport = -> [Pad]
  ExternalGeometry = -> [Binder010,Binder009,MultiTransform001]
  FullyConstrained = false
  MakeInternals = false
  MapMode = 5
  Placement = pos=(0,0,1.2) rot=(1,0,0;3.14159rad)
  sketch-geometry (6):
    g0: LineSegment StartX=43.45 StartY=-5.91 StartZ=0 EndX=27.25 EndY=-5.91 EndZ=0
    g1: GeomPoint [constr] X=28.5445 Y=-10.11 Z=0
    g2: LineSegment StartX=27.25 StartY=-5.91 StartZ=0 EndX=27.25 EndY=-14.31 EndZ=0
    g3: LineSegment StartX=27.25 StartY=-14.31 StartZ=0 EndX=42.3066 EndY=-14.31 EndZ=0
    g4: LineSegment StartX=43.45 StartY=-5.91 StartZ=0 EndX=43.45 EndY=-11.51 EndZ=0
    g5: ArcOfCircle CenterX=39.45 CenterY=-11.51 CenterZ=0 NormalX=0 NormalY=0 NormalZ=1 AngleXU=0 Radius=4 StartAngle=5.50779 EndAngle=6.28319
  constraints (13):
    c: Horizontal(g0)
    c: Coincident(g0,g-5)
    c: Coincident(g2,g0)
    c: Coincident(g2,g-5)
    c: Coincident(g3,g2)
    c: PointOnObject(g3,g-6)
    c: Horizontal(g3)
    c: Coincident(g4,g0)
    c: Coincident(g4,g-6)
    c: Vertical(g4)
    c: Coincident(g5,g4)
    c: Coincident(g5,g3)
    c: Vertical(g5,g-6)
FEATURE [PartDesign::Pocket] Pocket010  label="Logo pocket"
  BaseFeature = -> MultiTransform001
  Direction = (0,0,1)
  Length = 5
  Length2 = 5
  Placement = pos=(0,0,2.2) rot=(1,0,0;3.14159rad)
  Profile = -> Sketch015
  ReferenceAxis = -> Sketch015 [N_Axis]
  Suppressed = false
  Type = 1
FEATURE [PartDesign::SubShapeBinder] Binder011  label="LED matrix cap binder"
  BindCopyOnChange = 0
  BindMode = 0
  ClaimChildren = false
  Context = -> Body [Binder011.]
  Fuse = false
  MakeFace = true
  OffsetFill = false
  OffsetIntersection = false
  OffsetJoinType = 0
  OffsetOpenResult = false
  PartialLoad = false
  Relative = true
  Support = -> [Board_e6d008[Step_Models_e6d008.Top_e6d008.C13_C_0402_1005Metric_50b0befdca8e_ln_159.]]
  _Version = 2
FEATURE [Sketcher::SketchObject] Sketch016
  ArcFitTolerance = 1e-06
  AttachmentSupport = -> [Pad001]
  ExternalGeometry = -> [Binder011,Binder]
  FullyConstrained = true
  MakeInternals = false
  MapMode = 5
  Placement = pos=(0,-13.5,2.2) rot=(0,0.707107,-0.707107;3.14159rad)
  sketch-geometry (4):
    g0: LineSegment StartX=9.38 StartY=2.2 StartZ=0 EndX=9.38 EndY=1.6 EndZ=0
    g1: LineSegment StartX=9.38 StartY=1.6 StartZ=0 EndX=10.58 EndY=1.6 EndZ=0
    g2: LineSegment StartX=10.58 StartY=1.6 StartZ=0 EndX=10.58 EndY=2.2 EndZ=0
    g3: LineSegment StartX=10.58 StartY=2.2 StartZ=0 EndX=9.38 EndY=2.2 EndZ=0
  constraints (12):
    c: Coincident(g0,g1)
    c: Coincident(g1,g2)
    c: Coincident(g2,g3)
    c: Coincident(g3,g0)
    c: Vertical(g0)
    c: Vertical(g2)
    c: Horizontal(g1)
    c: Horizontal(g3)
    c: DistanceY(g1,g-4) = 0.1
    c: DistanceX(g-4,g1) = 0.1
    c: PointOnObject(g0,g-5)
    c: DistanceX(g0,g-3) = 0.1
FEATURE [PartDesign::Pocket] Pocket011  label="LED matrix cap space"
  BaseFeature = -> Pocket010
  Direction = (0,1,2e-16)
  Length = 0
  Length2 = 5
  Placement = pos=(0,0,2.2) rot=(1,0,0;3.14159rad)
  Profile = -> Sketch016
  ReferenceAxis = -> Sketch016 [N_Axis]
  Refine = true
  Suppressed = false
  Type = 3
  UpToFace = -> Pad001 [Face96]
FEATURE [PartDesign::LinearPattern] LinearPattern006  label="Cap space pattern"
  BaseFeature = -> Pocket011
  Direction = -> X_Axis016
  Length = 21
  Mode = 1
  Occurrences = 8
  Offset = 3
  Originals = -> [Pocket011]
  Placement = pos=(0,0,2.2) rot=(1,0,0;3.14159rad)
  Suppressed = false
  TransformMode = 0
FEATURE [Sketcher::SketchObject] Sketch017
  ArcFitTolerance = 1e-06
  AttachmentSupport = -> [Pocket001]
  ExternalGeometry = -> [Pocket001]
  FullyConstrained = true
  MakeInternals = false
  MapMode = 5
  Placement = pos=(0,0,2.2) rot=(0,0,1;0rad)
  sketch-geometry (26):
    g0: ArcOfCircle CenterX=-39.45 CenterY=11.51 CenterZ=0 NormalX=0 NormalY=0 NormalZ=1 AngleXU=0 Radius=6.87587 StartAngle=1.96203 EndAngle=2.76048
    g1: ArcOfCircle CenterX=-44.4269 CenterY=13.5043 CenterZ=0 NormalX=0 NormalY=0 NormalZ=1 AngleXU=0 Radius=1.51427 StartAngle=2.76048 EndAngle=4.71239
    g2: ArcOfCircle CenterX=-41.5 CenterY=16.4797 CenterZ=0 NormalX=0 NormalY=0 NormalZ=1 AngleXU=0 Radius=1.5 StartAngle=0 EndAngle=1.96203
    g3: ArcOfCircle CenterX=-39.45 CenterY=-11.51 CenterZ=0 NormalX=0 NormalY=0 NormalZ=1 AngleXU=0 Radius=6.72015 StartAngle=3.43305 EndAngle=4.42093
    g4: ArcOfCircle CenterX=39.45 CenterY=11.51 CenterZ=0 NormalX=0 NormalY=0 NormalZ=1 AngleXU=0 Radius=6.72015 StartAngle=0.291457 EndAngle=1.27934
    g5: ArcOfCircle CenterX=39.45 CenterY=-11.51 CenterZ=0 NormalX=0 NormalY=0 NormalZ=1 AngleXU=0 Radius=6.72015 StartAngle=5.00385 EndAngle=5.99173
    g6: ArcOfCircle CenterX=-44.45 CenterY=-13.01 CenterZ=0 NormalX=0 NormalY=0 NormalZ=1 AngleXU=0 Radius=1.5 StartAngle=1.5708 EndAngle=3.43305
    g7: ArcOfCircle CenterX=-40.95 CenterY=-16.51 CenterZ=0 NormalX=0 NormalY=0 NormalZ=1 AngleXU=0 Radius=1.5 StartAngle=4.42093 EndAngle=6.28319
    g8: ArcOfCircle CenterX=44.45 CenterY=-13.01 CenterZ=0 NormalX=0 NormalY=0 NormalZ=1 AngleXU=0 Radius=1.5 StartAngle=5.99173 EndAngle=7.85398
    g9: ArcOfCircle CenterX=40.95 CenterY=-16.51 CenterZ=0 NormalX=0 NormalY=0 NormalZ=1 AngleXU=0 Radius=1.5 StartAngle=3.14159 EndAngle=5.00385
    g10: ArcOfCircle CenterX=44.45 CenterY=13.01 CenterZ=0 NormalX=0 NormalY=0 NormalZ=1 AngleXU=0 Radius=1.5 StartAngle=4.71239 EndAngle=6.57464
    g11: ArcOfCircle CenterX=40.95 CenterY=16.51 CenterZ=0 NormalX=0 NormalY=0 NormalZ=1 AngleXU=0 Radius=1.5 StartAngle=1.27934 EndAngle=3.14159
    g12: ArcOfCircle CenterX=-39.45 CenterY=11.51 CenterZ=0 NormalX=0 NormalY=0 NormalZ=1 AngleXU=0 Radius=5 StartAngle=1.68102 EndAngle=3.04544
    g13: ArcOfCircle CenterX=-39.45 CenterY=-11.51 CenterZ=0 NormalX=0 NormalY=0 NormalZ=1 AngleXU=0 Radius=5 StartAngle=3.14159 EndAngle=4.71239
    g14: ArcOfCircle CenterX=39.45 CenterY=-11.51 CenterZ=0 NormalX=0 NormalY=0 NormalZ=1 AngleXU=0 Radius=5 StartAngle=4.71239 EndAngle=6.28319
    g15: ArcOfCircle CenterX=39.45 CenterY=11.51 CenterZ=0 NormalX=0 NormalY=0 NormalZ=1 AngleXU=0 Radius=5 StartAngle=4e-16 EndAngle=1.5708
    g16: GeomPoint [constr] X=1.95e-14 Y=16.51 Z=0
    g17: GeomPoint [constr] X=1.95e-14 Y=-16.51 Z=0
    g18: LineSegment StartX=5 StartY=16.51 StartZ=0 EndX=-5 EndY=16.51 EndZ=0
    g19: ArcOfCircle CenterX=-3.5 CenterY=16.51 CenterZ=0 NormalX=0 NormalY=0 NormalZ=1 AngleXU=0 Radius=1.5 StartAngle=1.5708 EndAngle=3.14159
    g20: LineSegment StartX=-3.5 StartY=18.01 StartZ=0 EndX=3.5 EndY=18.01 EndZ=0
    g21: ArcOfCircle CenterX=3.5 CenterY=16.51 CenterZ=0 NormalX=0 NormalY=0 NormalZ=1 AngleXU=0 Radius=1.5 StartAngle=0 EndAngle=1.5708
    g22: LineSegment StartX=-5 StartY=-16.51 StartZ=0 EndX=5 EndY=-16.51 EndZ=0
    g23: ArcOfCircle CenterX=3.5 CenterY=-16.51 CenterZ=0 NormalX=0 NormalY=0 NormalZ=1 AngleXU=0 Radius=1.5 StartAngle=4.71239 EndAngle=6.28319
    g24: LineSegment StartX=3.5 StartY=-18.01 StartZ=0 EndX=-3.5 EndY=-18.01 EndZ=0
    g25: ArcOfCircle CenterX=-3.5 CenterY=-16.51 CenterZ=0 NormalX=0 NormalY=0 NormalZ=1 AngleXU=0 Radius=1.5 StartAngle=3.14159 EndAngle=4.71239
  constraints (72):
    c: Tangent(g1,g0) = -1.5708
    c: Vertical(g1,g1)
    c: Coincident(g1,g-3)
    c: Coincident(g2,g-3)
    c: Tangent(g2,g0) = -1.5708
    c: Horizontal(g2,g2)
    c: DistanceX(g2,g2) = 1.5
    c: Coincident(g3,g-4)
    c: Coincident(g4,g-6)
    c: Coincident(g6,g-4)
    c: Coincident(g7,g-4)
    c: Coincident(g8,g-5)
    c: Coincident(g9,g-5)
    c: Coincident(g10,g-6)
    c: Coincident(g11,g-6)
    c: Coincident(g13,g3)
    c: Coincident(g14,g5)
    c: Coincident(g14,g9)
    c: Coincident(g15,g10)
    c: Vertical(g6,g13)
    c: Horizontal(g7,g7)
    c: Horizontal(g9,g9)
    c: Vertical(g10,g10)
    c: Horizontal(g11,g11)
    c: Coincident(g4,g15)
    c: Equal(g6,g2)
    c: Tangent(g6,g3) = -1.5708
    c: Tangent(g7,g3) = -1.5708
    c: Equal(g2,g11)
    c: Tangent(g11,g4) = -1.5708
    c: Tangent(g10,g4) = -1.5708
    c: Tangent(g8,g5) = -1.5708
    c: Tangent(g9,g5) = -1.5708
    c: Equal(g2,g8)
    c: Coincident(g13,g6)
    c: Coincident(g2,g12)
    c: Coincident(g12,g1)
    c: Vertical(g13,g7)
    c: Coincident(g12,g0)
    c: Vertical(g0,g3)
    c: Vertical(g15,g11)
    c: Symmetric(g13,g9,g17)
    c: Vertical(g16,g17)
    c: Horizontal(g15,g16)
    c: Horizontal(g18)
    c: Coincident(g19,g20)
    c: Horizontal(g20)
    c: Coincident(g21,g18)
    c: Horizontal(g21,g18)
    c: Vertical(g21,g20)
    c: Coincident(g20,g21)
    c: Vertical(g19,g19)
    c: Horizontal(g19,g19)
    c: Coincident(g18,g19)
    c: Symmetric(g18,g18,g16)
    c: Equal(g2,g19)
    c: DistanceX(g18,g18) = 10
    c: Coincident(g23,g24)
    c: Tangent(g24,g25) = 1.5708
    c: Coincident(g25,g22)
    c: Symmetric(g22,g22,g17)
    c: Horizontal(g22)
    c: Horizontal(g24)
    c: Horizontal(g25,g22)
    c: Horizontal(g23,g22)
    c: Vertical(g23,g23)
    c: Equal(g18,g22)
    c: Equal(g19,g25)
    c: Coincident(g23,g22)
    c: Coincident(g14,g8)
    c: Equal(g-5,g14)
    c: Vertical(g8,g8)
FEATURE [PartDesign::Pad] Pad007  label="Pads around PCBs"
  BaseFeature = -> LinearPattern006
  Direction = (0,0,1)
  Length = 3
  Length2 = 0.9
  Placement = pos=(0,0,2.2) rot=(1,0,0;3.14159rad)
  Profile = -> Sketch017
  ReferenceAxis = -> Sketch017 [N_Axis]
  Refine = true
  Reversed = true
  Suppressed = false
  Type = 4
FEATURE [PartDesign::Chamfer] Chamfer
  Angle = 45
  Base = -> Pad007 [Edge1569,Edge1991,Edge1578,Edge1992,Edge1587,Edge1993,Edge1604,Edge1609,Edge1520,Edge1995,Edge1994,Edge1949]
  BaseFeature = -> Pad007
  ChamferType = 0
  FlipDirection = false
  Placement = pos=(0,0,2.2) rot=(1,0,0;3.14159rad)
  Refine = true
  Size = 0.6
  Size2 = 1
  SupportTransform = false
  Suppressed = false
  UseAllEdges = false
FEATURE [PartDesign::Body] Body
  AllowCompound = false
  Group = -> [Binder011,Binder009,Binder010,Binder002,Binder001,DatumPlane001,Binder,DatumPlane,Sketch,Sketch001,Pad,Pad001,Sketch002,Pocket,MultiTransform,LinearPattern,LinearPattern001,Sketch003,Pad002,Sketch004,Pad003,Sketch005,Pocket001,Sketch014,Pad006,MultiTransform001,LinearPattern004,LinearPattern005,Sketch015,Pocket010,Sketch016,Pocket011,LinearPattern006,Sketch017,Pad007,Chamfer]
  Origin = -> Origin016
  Tip = -> Chamfer
COMPONENT P5 — recipe-attached ("DirCluster", modeled in this document).
Construction recipe (the document's own serialized feature program — sketch geometry with constraints, then the solid features built on it; lengths are millimeters unless a unit is written):

FEATURE [PartDesign::SubShapeBinder] Binder003
  BindCopyOnChange = 0
  BindMode = 0
  ClaimChildren = false
  Context = -> Body001 [Binder003.]
  Fuse = false
  MakeFace = true
  OffsetFill = false
  OffsetIntersection = false
  OffsetJoinType = 0
  OffsetOpenResult = false
  PartialLoad = false
  Relative = true
  Support = -> [Body[Pocket001.]]
  _Version = 2
FEATURE [PartDesign::Plane] DatumPlane002
  AttachmentSupport = -> [Binder003]
  Length = 80.1188
  MapMode = 5
  Placement = pos=(0,0,1.2) rot=(1,0,0;3.14159rad)
  ResizeMode = 0
  Width = 61.6979
FEATURE [Sketcher::SketchObject] Sketch006
  ArcFitTolerance = 1e-06
  AttachmentSupport = -> [DatumPlane002]
  ExternalGeometry = -> [Binder003]
  FullyConstrained = true
  MakeInternals = false
  MapMode = 5
  Placement = pos=(0,0,1.2) rot=(1,0,0;3.14159rad)
  sketch-geometry (12):
    g0: ArcOfCircle CenterX=-33.45 CenterY=-0.49 CenterZ=0 NormalX=0 NormalY=0 NormalZ=1 AngleXU=0 Radius=4 StartAngle=3.14159 EndAngle=6.28319
    g1: ArcOfCircle CenterX=-27.45 CenterY=5.51 CenterZ=0 NormalX=0 NormalY=0 NormalZ=1 AngleXU=0 Radius=4 StartAngle=4.71239 EndAngle=7.85398
    g2: LineSegment StartX=-29.45 StartY=-0.49 StartZ=0 EndX=-29.45 EndY=1.51 EndZ=0
    g3: LineSegment StartX=-27.45 StartY=1.51 StartZ=0 EndX=-29.45 EndY=1.51 EndZ=0
    g4: LineSegment StartX=-37.45 StartY=-0.49 StartZ=0 EndX=-37.45 EndY=1.51 EndZ=0
    g5: LineSegment StartX=-27.45 StartY=9.51 StartZ=0 EndX=-29.45 EndY=9.51 EndZ=0
    g6: LineSegment StartX=-37.45 StartY=1.51 StartZ=0 EndX=-39.45 EndY=1.51 EndZ=0
    g7: LineSegment StartX=-29.45 StartY=9.51 StartZ=0 EndX=-29.45 EndY=11.51 EndZ=0
    g8: LineSegment StartX=-37.45 StartY=9.51 StartZ=0 EndX=-39.45 EndY=9.51 EndZ=0
    g9: LineSegment StartX=-37.45 StartY=9.51 StartZ=0 EndX=-37.45 EndY=11.51 EndZ=0
    g10: ArcOfCircle CenterX=-33.45 CenterY=11.51 CenterZ=0 NormalX=0 NormalY=0 NormalZ=1 AngleXU=0 Radius=4 StartAngle=2.1e-15 EndAngle=3.14159
    g11: ArcOfCircle CenterX=-39.45 CenterY=5.51 CenterZ=0 NormalX=0 NormalY=0 NormalZ=1 AngleXU=0 Radius=4 StartAngle=1.5708 EndAngle=4.71239
  constraints (38):
    c: Coincident(g0,g-3)
    c: Coincident(g1,g-4)
    c: Vertical(g1,g1)
    c: Vertical(g1,g1)
    c: Horizontal(g0,g0)
    c: Horizontal(g0,g0)
    c: Equal(g0,g1)
    c: DistanceX(g-3,g0) = 0.2
    c: Coincident(g2,g0)
    c: Vertical(g2)
    c: Coincident(g3,g1)
    c: Coincident(g3,g2)
    c: Horizontal(g3)
    c: Coincident(g4,g0)
    c: Vertical(g4)
    c: Coincident(g5,g1)
    c: Horizontal(g5)
    c: Vertical(g5,g2)
    c: Horizontal(g4,g2)
    c: Coincident(g6,g4)
    c: Horizontal(g6)
    c: Coincident(g7,g5)
    c: Vertical(g7)
    c: Equal(g2,g7)
    c: Equal(g6,g3)
    c: Horizontal(g8)
    c: Coincident(g9,g8)
    c: Vertical(g9)
    c: Horizontal(g8,g5)
    c: Vertical(g8,g4)
    c: Vertical(g8,g6)
    c: Horizontal(g9,g7)
    c: Coincident(g10,g9)
    c: Coincident(g10,g7)
    c: Symmetric(g9,g7,g10)
    c: Coincident(g11,g6)
    c: Coincident(g11,g8)
    c: Symmetric(g6,g8,g11)
FEATURE [PartDesign::SubShapeBinder] Binder004
  BindCopyOnChange = 0
  BindMode = 0
  ClaimChildren = false
  Context = -> Body001 [Binder004.]
  Fuse = false
  MakeFace = true
  OffsetFill = false
  OffsetIntersection = false
  OffsetJoinType = 0
  OffsetOpenResult = false
  PartialLoad = false
  Relative = true
  Support = -> [Board_83e9[Board_Geoms_83e9.Pcb_83e9.Face32]]
  _Version = 2
FEATURE [PartDesign::Pad] Pad004
  Direction = (0,0,-1)
  Length = 10
  Length2 = 10
  Placement = pos=(0,0,1.2) rot=(1,0,0;3.14159rad)
  Profile = -> Sketch006
  ReferenceAxis = -> Sketch006 [N_Axis]
  Reversed = true
  Suppressed = false
  Type = 3
  UpToFace = -> Binder004 [Face1]
FEATURE [PartDesign::Point] DatumPoint
  AttacherType = Attacher::AttachEnginePoint
  AttachmentSupport = -> [Pad004]
  MapMode = 37
  Placement = pos=(-33.45,-11.51,2.2) rot=(0,0,1;0rad)
FEATURE [PartDesign::Line] DatumLine
  AttacherType = Attacher::AttachEngineLine
  AttachmentSupport = -> [DatumPoint,Pad004]
  Length = 20
  MapMode = 46
  Placement = pos=(-33.45,-11.51,2.2) rot=(0,0,1;3.14159rad)
  ResizeMode = 0
FEATURE [PartDesign::Point] DatumPoint001
  AttacherType = Attacher::AttachEnginePoint
  AttachmentSupport = -> [Pad004]
  MapMode = 37
  Placement = pos=(-33.45,-5.51,2.2) rot=(0,0,1;0rad)
FEATURE [PartDesign::Plane] DatumPlane003
  AttachmentSupport = -> [DatumLine,DatumPoint001]
  Length = 60
  MapMode = 13
  Placement = pos=(-33.45,-9.51,2.53333) rot=(0.57735,-0.57735,-0.57735;2.0944rad)
  ResizeMode = 0
  Width = 60
FEATURE [Sketcher::SketchObject] Sketch007
  ArcFitTolerance = 1e-06
  AttachmentSupport = -> [DatumPlane003]
  ExternalGeometry = -> [Pad004]
  FullyConstrained = true
  MakeInternals = false
  MapMode = 5
  Placement = pos=(-33.45,-9.51,2.53333) rot=(0.57735,-0.57735,-0.57735;2.0944rad)
  sketch-geometry (5):
    g0: LineSegment StartX=2 StartY=-0.333333 StartZ=0 EndX=4.9 EndY=-0.333333 EndZ=0
    g1: LineSegment StartX=4.9 StartY=-0.333333 StartZ=0 EndX=4.9 EndY=0.766667 EndZ=0
    g2: LineSegment StartX=2 StartY=-0.333333 StartZ=0 EndX=2 EndY=1.06667 EndZ=0
    g3: ArcOfCircle CenterX=4.74911 CenterY=0.766667 CenterZ=0 NormalX=0 NormalY=0 NormalZ=1 AngleXU=0 Radius=0.150885 StartAngle=0 EndAngle=1.46242
    g4: ArcOfCircle CenterX=2 CenterY=-24.5004 CenterZ=0 NormalX=0 NormalY=0 NormalZ=1 AngleXU=0 Radius=25.5671 StartAngle=1.46242 EndAngle=1.5708
  constraints (15):
    c: Distance(g0) = 2.9
    c: Coincident(g0,g-3)
    c: Horizontal(g0)
    c: Coincident(g1,g0)
    c: Vertical(g1)
    c: Distance(g2) = 1.4
    c: Coincident(g2,g0)
    c: Vertical(g2)
    c: Coincident(g3,g1)
    c: Horizontal(g3,g1)
    c: Coincident(g4,g2)
    c: Tangent(g4,g3) = -1.5708
    c: PointOnObject(g4,g-3)
    c: DistanceY(g0,g1) = 1.1
    c: DistanceY(g1,g3) = 0.15
FEATURE [PartDesign::Revolution] Revolution
  Angle = 360
  Angle2 = 60
  Axis = (0,0,1)
  Base = (-33.45,-11.51,2.2)
  BaseFeature = -> Pad004
  Placement = pos=(0,0,1.2) rot=(1,0,0;3.14159rad)
  Profile = -> Sketch007
  ReferenceAxis = -> DatumLine
  Refine = true
  Reversed = true
  Suppressed = false
  Type = 0
FEATURE [PartDesign::Line] DatumLine001
  AttacherType = Attacher::AttachEngineLine
  AttachmentSupport = -> [Revolution,DatumPoint001]
  Length = 20
  MapMode = 46
  Placement = pos=(-33.45,-5.51,2.2) rot=(0,0,1;3.14159rad)
  ResizeMode = 0
FEATURE [PartDesign::PolarPattern] PolarPattern
  Angle = 360
  Axis = -> DatumLine001
  BaseFeature = -> Revolution
  Mode = 0
  Occurrences = 4
  Offset = 120
  Originals = -> [Revolution]
  Placement = pos=(0,0,1.2) rot=(1,0,0;3.14159rad)
  Suppressed = false
  TransformMode = 0
FEATURE [Sketcher::SketchObject] Sketch008
  ArcFitTolerance = 1e-06
  AttachmentSupport = -> [PolarPattern]
  ExternalGeometry = -> [DatumPoint]
  FullyConstrained = true
  MakeInternals = false
  MapMode = 5
  Placement = pos=(0,0,1.2) rot=(1,0,0;3.14159rad)
  sketch-geometry (1):
    g0: Circle CenterX=-33.45 CenterY=11.51 CenterZ=0 NormalX=0 NormalY=0 NormalZ=1 AngleXU=0 Radius=2.05
  constraints (2):
    c: Coincident(g0,g-3)
    c: Diameter(g0) = 4.1
FEATURE [PartDesign::Pocket] Pocket002
  BaseFeature = -> PolarPattern
  Direction = (0,0,1)
  Length = 0.32
  Length2 = 5
  Placement = pos=(0,0,1.2) rot=(1,0,0;3.14159rad)
  Profile = -> Sketch008
  ReferenceAxis = -> Sketch008 [N_Axis]
  Suppressed = false
  Type = 0
FEATURE [PartDesign::PolarPattern] PolarPattern001
  Angle = 360
  Axis = -> DatumLine001
  BaseFeature = -> Pocket002
  Mode = 0
  Occurrences = 4
  Offset = 120
  Originals = -> [Pocket002]
  Placement = pos=(0,0,1.2) rot=(1,0,0;3.14159rad)
  Suppressed = false
  TransformMode = 0
FEATURE [Sketcher::SketchObject] Sketch009
  ArcFitTolerance = 1e-06
  AttachmentOffset = pos=(0,0,0.9) rot=(0,0,1;0rad)
  AttachmentSupport = -> [PolarPattern001]
  ExternalGeometry = -> [PolarPattern001]
  FullyConstrained = true
  MakeInternals = false
  MapMode = 5
  Placement = pos=(0,-4e-16,3.1) rot=(0,0,1;0rad)
  sketch-geometry (4):
    g0: LineSegment StartX=-32.3675 StartY=-10.885 StartZ=0 EndX=-34.5325 EndY=-10.885 EndZ=0
    g1: LineSegment StartX=-34.5325 StartY=-10.885 StartZ=0 EndX=-33.45 EndY=-12.76 EndZ=0
    g2: LineSegment StartX=-33.45 StartY=-12.76 StartZ=0 EndX=-32.3675 EndY=-10.885 EndZ=0
    g3: Circle [constr] CenterX=-33.45 CenterY=-11.51 CenterZ=0 NormalX=0 NormalY=0 NormalZ=1 AngleXU=0 Radius=1.25
  constraints (11):
    c: Coincident(g0,g1)
    c: Coincident(g1,g2)
    c: Coincident(g2,g0)
    c: Equal(g0,g1)
    c: Equal(g0,g2)
    c: PointOnObject(g0,g3)
    c: PointOnObject(g1,g3)
    c: PointOnObject(g2,g3)
    c: Radius(g3) = 1.25
    c: Coincident(g3,g-3)
    c: Horizontal(g0)
FEATURE [PartDesign::Pocket] Pocket003
  BaseFeature = -> PolarPattern001
  Direction = (0,0,-1)
  Length = 5
  Length2 = 5
  Placement = pos=(0,0,1.2) rot=(1,0,0;3.14159rad)
  Profile = -> Sketch009
  ReferenceAxis = -> Sketch009 [N_Axis]
  Reversed = true
  Suppressed = false
  Type = 1
FEATURE [PartDesign::PolarPattern] PolarPattern002
  Angle = 360
  Axis = -> DatumLine001
  BaseFeature = -> Pocket003
  Mode = 0
  Occurrences = 4
  Offset = 120
  Originals = -> [Pocket003]
  Placement = pos=(0,0,1.2) rot=(1,0,0;3.14159rad)
  Refine = true
  Suppressed = false
  TransformMode = 0
FEATURE [PartDesign::Body] Body001  label="DirCluster"
  AllowCompound = false
  Group = -> [Binder003,DatumPlane002,Binder004,Sketch006,Pad004,DatumPoint,DatumLine,DatumPoint001,DatumPlane003,Sketch007,Revolution,DatumLine001,PolarPattern,Sketch008,Pocket002,PolarPattern001,Sketch009,Pocket003,PolarPattern002]
  Origin = -> Origin017
  Tip = -> PolarPattern002
COMPONENT P6 — recipe-attached ("CommandCluster", modeled in this document).
Construction recipe (the document's own serialized feature program — sketch geometry with constraints, then the solid features built on it; lengths are millimeters unless a unit is written):

FEATURE [PartDesign::FeatureBase] Clone
  BaseFeature = -> PolarPattern001
  Placement = pos=(0,-9e-16,1.2) rot=(1,0,0;3.14159rad)
  Suppressed = false
FEATURE [Part::Part2DObjectPython] ShapeString  # Draft 2D object (typed FeaturePython)
  AttachmentOffset = pos=(0.9,1,0) rot=(0,0,1;3.14159rad)
  AttachmentSupport = -> [Clone]
  FontFile = <path>
  Fuse = false
  Justification = 6
  JustificationReference = 0
  KeepLeftMargin = false
  MakeFace = true
  MapMode = 6
  ObliqueAngle = 0
  Placement = pos=(-34.35,-12.51,3.6) rot=(0,0,1;0rad)
  ScaleToSize = true
  Size = 2
  String = A
  Tracking = 0
FEATURE [PartDesign::Pocket] Pocket004
  BaseFeature = -> Clone
  Direction = (0,0,-1)
  Length = 0.2
  Length2 = 5
  Placement = pos=(0,-9e-16,1.2) rot=(1,0,0;3.14159rad)
  Profile = -> ShapeString
  ReferenceAxis = -> ShapeString [N_Axis]
  Suppressed = false
  Type = 0
FEATURE [Part::Part2DObjectPython] ShapeString001  # Draft 2D object (typed FeaturePython)
  AttachmentOffset = pos=(1,-0.6,0) rot=(0,0,1;1.5708rad)
  AttachmentSupport = -> [Clone]
  FontFile = <path>
  Fuse = false
  Justification = 6
  JustificationReference = 0
  KeepLeftMargin = false
  MakeFace = true
  MapMode = 6
  ObliqueAngle = 0
  Placement = pos=(-28.05,-6.51,3.6) rot=(0,0,1;0rad)
  ScaleToSize = true
  Size = 2
  String = B
  Tracking = 0
FEATURE [PartDesign::Pocket] Pocket005
  BaseFeature = -> Pocket004
  Direction = (0,0,-1)
  Length = 0.2
  Length2 = 5
  Placement = pos=(0,-9e-16,1.2) rot=(1,0,0;3.14159rad)
  Profile = -> ShapeString001
  ReferenceAxis = -> ShapeString001 [N_Axis]
  Suppressed = false
  Type = 0
FEATURE [Part::Part2DObjectPython] ShapeString002  # Draft 2D object (typed FeaturePython)
  AttachmentOffset = pos=(-1,0.9,0) rot=(0,0,1;-1.5708rad)
  AttachmentSupport = -> [Pocket005]
  FontFile = <path>
  Fuse = false
  Justification = 6
  JustificationReference = 0
  KeepLeftMargin = false
  MakeFace = true
  MapMode = 6
  ObliqueAngle = 0
  Placement = pos=(-40.35,-6.51,3.6) rot=(0,0,1;0rad)
  ScaleToSize = true
  Size = 2
  String = X
  Tracking = 0
FEATURE [PartDesign::Pocket] Pocket006
  BaseFeature = -> Pocket005
  Direction = (0,0,-1)
  Length = 0.2
  Length2 = 5
  Placement = pos=(0,-9e-16,1.2) rot=(1,0,0;3.14159rad)
  Profile = -> ShapeString002
  ReferenceAxis = -> ShapeString002 [N_Axis]
  Suppressed = false
  Type = 0
FEATURE [Part::Part2DObjectPython] ShapeString003  # Draft 2D object (typed FeaturePython)
  AttachmentOffset = pos=(-0.92,-1,0) rot=(0,0,1;0rad)
  AttachmentSupport = -> [Pocket006]
  FontFile = <path>
  Fuse = false
  Justification = 6
  JustificationReference = 0
  KeepLeftMargin = false
  MakeFace = true
  MapMode = 6
  ObliqueAngle = 0
  Placement = pos=(-34.37,-0.51,3.6) rot=(0,0,1;0rad)
  ScaleToSize = true
  Size = 2
  String = Y
  Tracking = 0
FEATURE [PartDesign::Pocket] Pocket007
  BaseFeature = -> Pocket006
  Direction = (0,0,-1)
  Length = 0.2
  Length2 = 5
  Placement = pos=(0,-9e-16,1.2) rot=(1,0,0;3.14159rad)
  Profile = -> ShapeString003
  ReferenceAxis = -> ShapeString003 [N_Axis]
  Suppressed = false
  Type = 0
FEATURE [PartDesign::Body] Body004  label="CommandCluster"
  AllowCompound = false
  Group = -> [Clone,ShapeString,Pocket004,ShapeString001,Pocket005,ShapeString002,Pocket006,ShapeString003,Pocket007]
  Origin = -> Origin020
  Placement = pos=(66.9,0,0) rot=(0,0,1;0rad)
  Tip = -> Pocket007
COMPONENT P7 — recipe-attached ("SelectStartCluster", modeled in this document).
Construction recipe (the document's own serialized feature program — sketch geometry with constraints, then the solid features built on it; lengths are millimeters unless a unit is written):

FEATURE [PartDesign::SubShapeBinder] Binder005
  BindCopyOnChange = 0
  BindMode = 0
  ClaimChildren = false
  Context = -> Body005 [Binder005.]
  Fuse = false
  MakeFace = true
  OffsetFill = false
  OffsetIntersection = false
  OffsetJoinType = 0
  OffsetOpenResult = false
  PartialLoad = false
  Relative = true
  Support = -> [Body[Pocket001.]]
  _Version = 2
FEATURE [PartDesign::Plane] DatumPlane004
  AttachmentSupport = -> [Binder005]
  Length = 66.8326
  MapMode = 5
  Placement = pos=(0,0,1.2) rot=(1,0,0;3.14159rad)
  ResizeMode = 0
  Width = 60.6045
FEATURE [Sketcher::SketchObject] Sketch010
  ArcFitTolerance = 1e-06
  AttachmentSupport = -> [DatumPlane004]
  ExternalGeometry = -> [Binder005]
  FullyConstrained = true
  MakeInternals = false
  MapMode = 5
  Placement = pos=(0,0,1.2) rot=(1,0,0;3.14159rad)
  sketch-geometry (4):
    g0: ArcOfCircle CenterX=18.55 CenterY=-10.11 CenterZ=0 NormalX=0 NormalY=0 NormalZ=1 AngleXU=0 Radius=4 StartAngle=1.5708 EndAngle=4.71239
    g1: ArcOfCircle CenterX=27.25 CenterY=-10.11 CenterZ=0 NormalX=0 NormalY=0 NormalZ=1 AngleXU=0 Radius=4 StartAngle=4.71239 EndAngle=7.85398
    g2: LineSegment StartX=18.55 StartY=-6.11 StartZ=0 EndX=27.25 EndY=-6.11 EndZ=0
    g3: LineSegment StartX=18.55 StartY=-14.11 StartZ=0 EndX=27.25 EndY=-14.11 EndZ=0
  constraints (8):
    c: Tangent(g0,g2) = 1.5708
    c: Tangent(g0,g3) = -1.5708
    c: Tangent(g1,g2) = 1.5708
    c: Tangent(g1,g3) = -1.5708
    c: Equal(g0,g1)
    c: Coincident(g1,g-4)
    c: Coincident(g0,g-3)
    c: DistanceY(g-4,g1) = 0.2
FEATURE [PartDesign::SubShapeBinder] Binder006
  BindCopyOnChange = 0
  BindMode = 0
  ClaimChildren = false
  Context = -> Body005 [Binder006.]
  Fuse = false
  MakeFace = true
  OffsetFill = false
  OffsetIntersection = false
  OffsetJoinType = 0
  OffsetOpenResult = false
  PartialLoad = false
  Relative = true
  Support = -> [Body[Pocket001.Face2]]
  _Version = 2
FEATURE [PartDesign::Pad] Pad005
  Direction = (0,0,-1)
  Length = 10
  Length2 = 10
  Placement = pos=(0,0,1.2) rot=(1,0,0;3.14159rad)
  Profile = -> Sketch010
  ReferenceAxis = -> Sketch010 [N_Axis]
  Suppressed = false
  Type = 3
  UpToFace = -> Binder006 [Face1]
FEATURE [PartDesign::Point] DatumPoint002
  AttacherType = Attacher::AttachEnginePoint
  AttachmentSupport = -> [Pad005]
  MapMode = 37
  Placement = pos=(18.55,10.11,1.2) rot=(0,0,1;0rad)
FEATURE [PartDesign::Line] DatumLine002
  AttacherType = Attacher::AttachEngineLine
  AttachmentSupport = -> [Pad005,DatumPoint002]
  Length = 20
  MapMode = 46
  Placement = pos=(18.55,10.11,1.2) rot=(1,0,0;3.14159rad)
  ResizeMode = 0
FEATURE [PartDesign::SubShapeBinder] Binder007
  BindCopyOnChange = 0
  BindMode = 0
  ClaimChildren = false
  Context = -> Body005 [Binder007.]
  Fuse = false
  MakeFace = true
  OffsetFill = false
  OffsetIntersection = false
  OffsetJoinType = 0
  OffsetOpenResult = false
  PartialLoad = false
  Relative = true
  Support = -> [Body001]
  _Version = 2
FEATURE [Sketcher::SketchObject] Sketch011
  ArcFitTolerance = 1e-06
  AttachmentSupport = -> [Pad005]
  ExternalGeometry = -> [DatumPoint002,Binder007]
  FullyConstrained = true
  MakeInternals = false
  MapMode = 5
  Placement = pos=(0,0,1.2) rot=(1,0,0;3.14159rad)
  sketch-geometry (1):
    g0: Circle CenterX=18.55 CenterY=-10.11 CenterZ=0 NormalX=0 NormalY=0 NormalZ=1 AngleXU=0 Radius=2.05
  constraints (2):
    c: Coincident(g0,g-3)
    c: Equal(g0,g-4)
FEATURE [PartDesign::Pocket] Pocket008
  BaseFeature = -> Pad005
  Direction = (0,0,1)
  Length = 0
  Length2 = 5
  Placement = pos=(0,0,1.2) rot=(1,0,0;3.14159rad)
  Profile = -> Sketch011
  ReferenceAxis = -> Sketch011 [N_Axis]
  Suppressed = false
  Type = 3
  UpToFace = -> Binder007 [Face35]
FEATURE [PartDesign::Point] DatumPoint003
  AttacherType = Attacher::AttachEnginePoint
  AttachmentSupport = -> [Pocket008]
  MapMode = 37
  Placement = pos=(27.25,10.11,1.2) rot=(0,0,1;0rad)
FEATURE [PartDesign::LinearPattern] LinearPattern002
  BaseFeature = -> Pocket008
  Direction = -> Sketch011 [H_Axis]
  Length = 8.7
  Mode = 1
  Occurrences = 2
  Offset = 8.7
  Originals = -> [Pocket008]
  Placement = pos=(0,0,1.2) rot=(1,0,0;3.14159rad)
  Suppressed = false
  TransformMode = 0
FEATURE [PartDesign::SubShapeBinder] Binder008
  BindCopyOnChange = 0
  BindMode = 0
  ClaimChildren = false
  Context = -> Body005 [Binder008.]
  Fuse = false
  MakeFace = true
  OffsetFill = false
  OffsetIntersection = false
  OffsetJoinType = 0
  OffsetOpenResult = false
  PartialLoad = false
  Relative = true
  Support = -> [Body001[Sketch007.]]
  _Version = 2
FEATURE [PartDesign::Point] DatumPoint004
  AttacherType = Attacher::AttachEnginePoint
  AttachmentSupport = -> [LinearPattern002]
  MapMode = 37
  Placement = pos=(18.55,10.11,2.2) rot=(0,0,1;0rad)
FEATURE [PartDesign::Line] DatumLine003
  AttacherType = Attacher::AttachEngineLine
  AttachmentSupport = -> [LinearPattern002]
  Length = 20
  MapMode = 29
  Placement = pos=(18.55,-3.0571e-12,2.2) rot=(1,0,0;1.5708rad)
  ResizeMode = 0
FEATURE [PartDesign::Plane] DatumPlane005
  AttachmentSupport = -> [DatumLine002,DatumLine003]
  Length = 60
  MapMode = 13
  Placement = pos=(18.55,6.74,1.2) rot=(-0.57735,0.57735,0.57735;4.18879rad)
  ResizeMode = 0
  Width = 60
FEATURE [Sketcher::SketchObject] Sketch012
  ArcFitTolerance = 1e-06
  AttachmentSupport = -> [DatumPlane005]
  ExternalGeometry = -> [DatumPoint004,Binder008]
  FullyConstrained = true
  MakeInternals = false
  MapMode = 5
  Placement = pos=(18.55,6.74,1.2) rot=(-0.57735,0.57735,0.57735;4.18879rad)
  sketch-geometry (5):
    g0: LineSegment StartX=-3.37 StartY=1 StartZ=0 EndX=-3.37 EndY=2.4 EndZ=0
    g1: LineSegment StartX=-3.37 StartY=1 StartZ=0 EndX=-0.47 EndY=1 EndZ=0
    g2: LineSegment StartX=-0.47 StartY=1 StartZ=0 EndX=-0.47 EndY=2.1 EndZ=0
    g3: ArcOfCircle CenterX=-0.620885 CenterY=2.1 CenterZ=0 NormalX=0 NormalY=0 NormalZ=1 AngleXU=0 Radius=0.150885 StartAngle=0 EndAngle=1.46241
    g4: ArcOfCircle CenterX=-3.37 CenterY=-23.1671 CenterZ=0 NormalX=0 NormalY=0 NormalZ=1 AngleXU=0 Radius=25.5671 StartAngle=1.46242 EndAngle=1.5708
  constraints (16):
    c: Coincident(g0,g-3)
    c: Vertical(g0)
    c: Coincident(g1,g0)
    c: Horizontal(g1)
    c: Equal(g1,g-6)
    c: Equal(g0,g-7)
    c: Coincident(g2,g1)
    c: Vertical(g2)
    c: Equal(g-5,g2)
    c: Coincident(g3,g2)
    c: Horizontal(g3,g2)
    c: Equal(g3,g-8)
    c: Coincident(g4,g3)
    c: Coincident(g4,g0)
    c: PointOnObject(g4,g0)
    c: Equal(g4,g-4)
FEATURE [PartDesign::Revolution] Revolution001
  Angle = 360
  Angle2 = 60
  Axis = (0,0,-1)
  Base = (18.55,10.11,1.2)
  BaseFeature = -> LinearPattern002
  Placement = pos=(0,0,1.2) rot=(1,0,0;3.14159rad)
  Profile = -> Sketch012
  ReferenceAxis = -> DatumLine002
  Suppressed = false
  Type = 0
FEATURE [PartDesign::LinearPattern] LinearPattern003
  BaseFeature = -> Revolution001
  Direction = -> Sketch012 [N_Axis]
  Length = 8.7
  Mode = 0
  Occurrences = 2
  Offset = 8.7
  Originals = -> [Revolution001]
  Placement = pos=(0,0,1.2) rot=(1,0,0;3.14159rad)
  Reversed = true
  Suppressed = false
  TransformMode = 0
FEATURE [PartDesign::Plane] DatumPlane006
  AttachmentSupport = -> [LinearPattern003]
  Length = 66.8326
  MapMode = 6
  Placement = pos=(27.25,10.11,3.6) rot=(0,0,1;3.14159rad)
  ResizeMode = 0
  Width = 60.6045
FEATURE [Sketcher::SketchObject] Sketch013
  ArcFitTolerance = 1e-06
  AttachmentSupport = -> [DatumPlane006]
  ExternalGeometry = -> [LinearPattern003]
  FullyConstrained = true
  MakeInternals = false
  MapMode = 5
  Placement = pos=(27.25,10.11,3.6) rot=(0,0,1;3.14159rad)
  sketch-geometry (16):
    g0: LineSegment StartX=1 StartY=1.73205 StartZ=0 EndX=-2 EndY=-2.9e-15 EndZ=0
    g1: LineSegment StartX=-2 StartY=-2.9e-15 StartZ=0 EndX=1 EndY=-1.73205 EndZ=0
    g2: LineSegment StartX=1 StartY=-1.73205 StartZ=0 EndX=1 EndY=1.73205 EndZ=0
    g3: Circle [constr] CenterX=0 CenterY=0 CenterZ=0 NormalX=0 NormalY=0 NormalZ=1 AngleXU=0 Radius=2
    g4: LineSegment StartX=7.2 StartY=0.375 StartZ=0 EndX=7.2 EndY=-0.375 EndZ=0
    g5: LineSegment StartX=7.2 StartY=-0.375 StartZ=0 EndX=10.2 EndY=-0.375 EndZ=0
    g6: LineSegment StartX=10.2 StartY=-0.375 StartZ=0 EndX=10.2 EndY=0.375 EndZ=0
    g7: LineSegment StartX=10.2 StartY=0.375 StartZ=0 EndX=7.2 EndY=0.375 EndZ=0
    g8: LineSegment StartX=7.2 StartY=1.5 StartZ=0 EndX=7.2 EndY=0.75 EndZ=0
    g9: LineSegment StartX=7.2 StartY=0.75 StartZ=0 EndX=10.2 EndY=0.75 EndZ=0
    g10: LineSegment StartX=10.2 StartY=0.75 StartZ=0 EndX=10.2 EndY=1.5 EndZ=0
    g11: LineSegment StartX=10.2 StartY=1.5 StartZ=0 EndX=7.2 EndY=1.5 EndZ=0
    g12: LineSegment StartX=7.2 StartY=-0.75 StartZ=0 EndX=7.2 EndY=-1.5 EndZ=0
    g13: LineSegment StartX=7.2 StartY=-1.5 StartZ=0 EndX=10.2 EndY=-1.5 EndZ=0
    g14: LineSegment StartX=10.2 StartY=-1.5 StartZ=0 EndX=10.2 EndY=-0.75 EndZ=0
    g15: LineSegment StartX=10.2 StartY=-0.75 StartZ=0 EndX=7.2 EndY=-0.75 EndZ=0
  constraints (45):
    c: Coincident(g0,g1)
    c: Coincident(g1,g2)
    c: Coincident(g2,g0)
    c: Equal(g0,g1)
    c: Equal(g0,g2)
    c: PointOnObject(g0,g3)
    c: PointOnObject(g1,g3)
    c: PointOnObject(g2,g3)
    c: Radius(g3) = 2
    c: Coincident(g3,g-1)
    c: Vertical(g2)
    c: Coincident(g4,g5)
    c: Coincident(g5,g6)
    c: Coincident(g6,g7)
    c: Coincident(g7,g4)
    c: Vertical(g4)
    c: Vertical(g6)
    c: Horizontal(g5)
    c: Horizontal(g7)
    c: Symmetric(g4,g5,g-3)
    c: DistanceX(g7,g7) = 3
    c: DistanceY(g6,g6) = 0.75
    c: Coincident(g8,g9)
    c: Coincident(g9,g10)
    c: Coincident(g10,g11)
    c: Coincident(g11,g8)
    c: Vertical(g8)
    c: Vertical(g10)
    c: Horizontal(g9)
    c: Horizontal(g11)
    c: Coincident(g12,g13)
    c: Coincident(g13,g14)
    c: Coincident(g14,g15)
    c: Coincident(g15,g12)
    c: Vertical(g12)
    c: Vertical(g14)
    c: Horizontal(g13)
    c: Horizontal(g15)
    c: Vertical(g9,g6)
    c: Equal(g11,g7)
    c: Equal(g10,g6)
    c: Vertical(g4,g12)
    c: Equal(g12,g4)
    c: Symmetric(g8,g13,g-3)
    c: DistanceY(g13,g10) = 3
FEATURE [PartDesign::Pocket] Pocket009
  BaseFeature = -> LinearPattern003
  Direction = (0,0,-1)
  Length = 0
  Length2 = 5
  Placement = pos=(0,0,1.2) rot=(1,0,0;3.14159rad)
  Profile = -> Sketch013
  ReferenceAxis = -> Sketch013 [N_Axis]
  Suppressed = false
  Type = 3
  UpToFace = -> Binder007 [Face49]
FEATURE [PartDesign::Body] Body005  label="SelectStartCluster"
  AllowCompound = false
  Group = -> [Binder007,Binder006,Binder005,DatumPlane004,Sketch010,Pad005,DatumPoint002,DatumLine002,Sketch011,Pocket008,DatumPoint003,LinearPattern002,Binder008,DatumPoint004,DatumLine003,DatumPlane005,Sketch012,Revolution001,LinearPattern003,DatumPlane006,Sketch013,Pocket009]
  Origin = -> Origin021
  Tip = -> Pocket009
PROVENANCE & LICENSES
A FreeCAD (.FCStd) document from a public repository crawl; recipes are the document's own serialized feature recipes (and, for linked parts, companion documents' recipes).
License: as declared in the source repository (recorded in the dataset sidecar).
